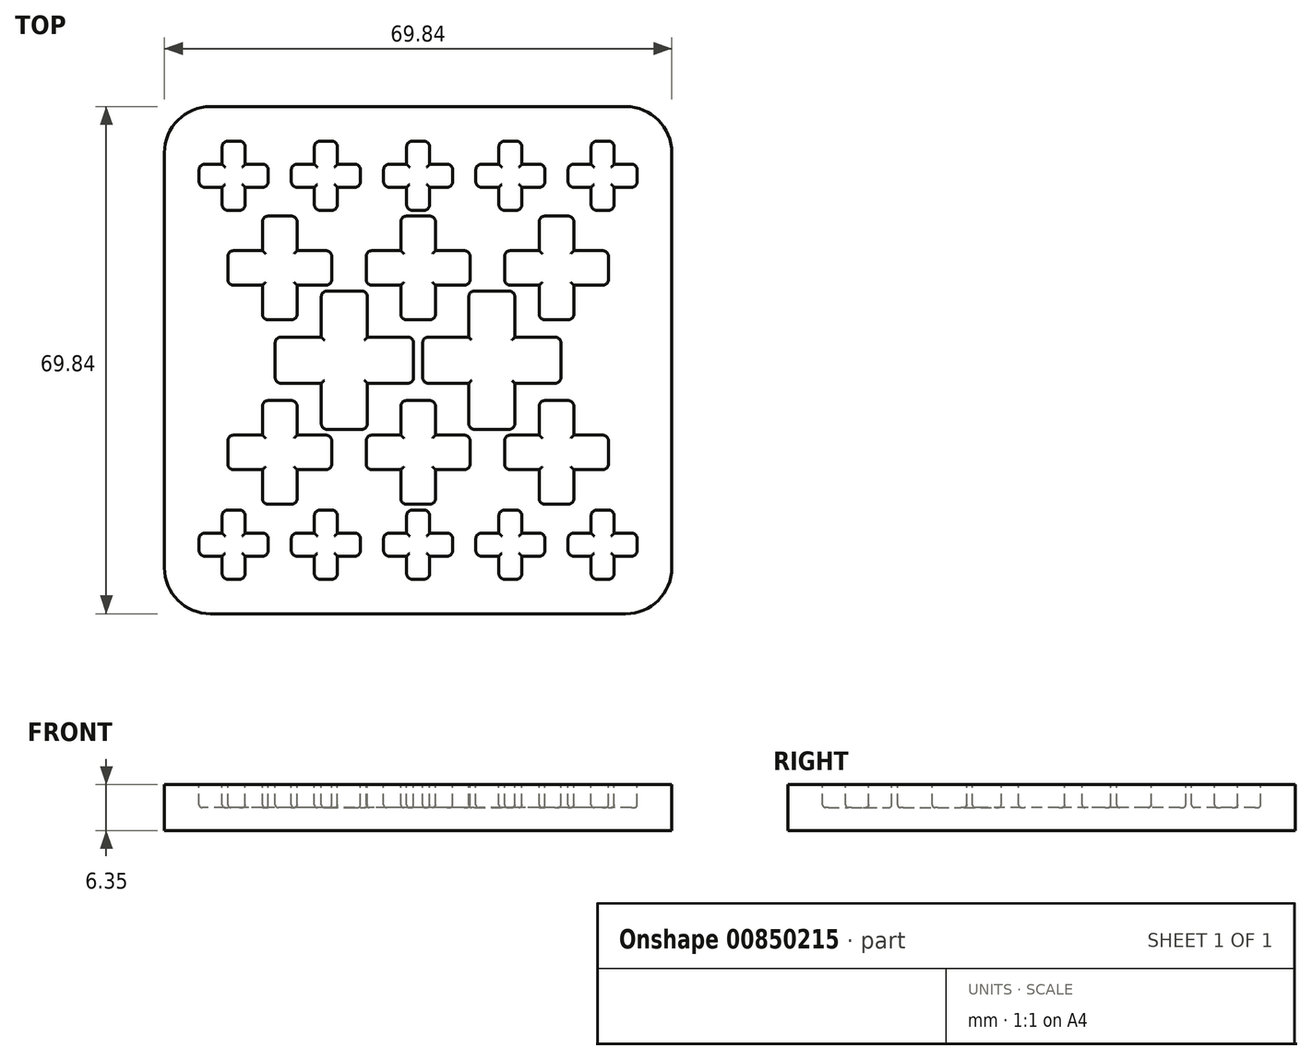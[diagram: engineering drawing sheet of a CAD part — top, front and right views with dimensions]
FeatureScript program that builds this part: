
annotation { "Feature Type Name" : "Feature", "Feature Type Description" : "" }
export const myFeature = defineFeature(function(context is Context, id is Id, definition is map)
    precondition{}
    {
        {
            var Q0;
            Q0=qCreatedBy(makeId("Top.planeOp"),FACE);
            var sketch = newSketch(context, id + "F0", { "sketchPlane" : qUnion([Q0])});
            skLineSegment(sketch, "E0.bottom", {"start": v(-28.57, 34.93) * mm, "end": v(28.58, 34.93) * mm});
            skLineSegment(sketch, "E0.top", {"start": v(-28.57, -34.93) * mm, "end": v(28.57, -34.93) * mm});
            skLineSegment(sketch, "E0.left", {"start": v(-34.92, 28.58) * mm, "end": v(-34.93, -28.57) * mm});
            skLineSegment(sketch, "E0.right", {"start": v(34.93, 28.58) * mm, "end": v(34.92, -28.57) * mm});
            skPoint(sketch, "E0.middle", {"position": v(0, 0) * mm});
            skPoint(sketch, "E1.visualSharp", {"position": v(-34.92, 34.93) * mm});
            skArc(sketch, "E1.filletArc", {"start": v(-28.57, 34.93) * mm, "mid": v(-33.07, 33.07) * mm, "end": v(-34.92, 28.58) * mm});
            skPoint(sketch, "E2.visualSharp", {"position": v(34.93, 34.93) * mm});
            skArc(sketch, "E2.filletArc", {"start": v(34.93, 28.58) * mm, "mid": v(33.07, 33.07) * mm, "end": v(28.58, 34.93) * mm});
            skPoint(sketch, "E3.visualSharp", {"position": v(34.92, -34.93) * mm});
            skArc(sketch, "E3.filletArc", {"start": v(28.57, -34.93) * mm, "mid": v(33.07, -33.07) * mm, "end": v(34.92, -28.57) * mm});
            skPoint(sketch, "E4.visualSharp", {"position": v(-34.93, -34.93) * mm});
            skArc(sketch, "E4.filletArc", {"start": v(-34.93, -28.57) * mm, "mid": v(-33.07, -33.07) * mm, "end": v(-28.57, -34.93) * mm});
            skSolve(sketch);
        }
        {
            var Q0;
            Q0 = qSketchRegion(id + "F0", true);
            extrude(context, id + "F1", {"entities" : qUnion([Q0]), "depth" : 6.35 * mm, "offsetDistance" : 25.4 * mm});
        }
        {
            var Q0;
            Q0=makeQuery(id+"F1.opExtrude","CAP_FACE",FACE,{"disambiguationData":[OSD([sQuery(id+"F0.wireOp",EDGE,"E0.bottom"),sQuery(id+"F0.wireOp",EDGE,"E0.top"),sQuery(id+"F0.wireOp",EDGE,"E0.left"),sQuery(id+"F0.wireOp",EDGE,"E0.right")])],"isStart":false});
            var sketch = newSketch(context, id + "F2", { "sketchPlane" : qUnion([Q0])});
            skLineSegment(sketch, "E5", {"start": v(0, 0) * mm, "end": v(0, 25.4) * mm, "construction": true});
            skLineSegment(sketch, "E6", {"start": v(0, 0) * mm, "end": v(0, 12.7) * mm, "construction": true});
            skLineSegment(sketch, "E7", {"start": v(0, 25.4) * mm, "end": v(-25.4, 25.4) * mm, "construction": true});
            skLineSegment(sketch, "E8", {"start": v(0, 12.7) * mm, "end": v(-19.05, 12.7) * mm, "construction": true});
            skLineSegment(sketch, "E9", {"start": v(0, 0) * mm, "end": v(-10.16, 0) * mm, "construction": true});
            skLineSegment(sketch, "E10.bottom", {"start": v(-24.6, 30.16) * mm, "end": v(-26.2, 30.16) * mm});
            skLineSegment(sketch, "E10.top", {"start": v(-24.6, 20.64) * mm, "end": v(-26.2, 20.64) * mm});
            skLineSegment(sketch, "E10.left", {"start": v(-23.81, 29.37) * mm, "end": v(-23.81, 21.43) * mm});
            skLineSegment(sketch, "E10.right", {"start": v(-26.99, 29.37) * mm, "end": v(-26.99, 21.43) * mm});
            skPoint(sketch, "E10.middle", {"position": v(-25.4, 25.4) * mm});
            skLineSegment(sketch, "E11.bottom", {"start": v(-21.43, 26.99) * mm, "end": v(-29.37, 26.99) * mm});
            skLineSegment(sketch, "E11.top", {"start": v(-21.43, 23.81) * mm, "end": v(-29.37, 23.81) * mm});
            skLineSegment(sketch, "E11.left", {"start": v(-20.64, 26.2) * mm, "end": v(-20.64, 24.6) * mm});
            skLineSegment(sketch, "E11.right", {"start": v(-30.16, 26.2) * mm, "end": v(-30.16, 24.6) * mm});
            skPoint(sketch, "E12.visualSharp", {"position": v(-26.99, 30.16) * mm});
            skArc(sketch, "E12.filletArc", {"start": v(-26.2, 30.16) * mm, "mid": v(-26.76, 29.93) * mm, "end": v(-26.99, 29.37) * mm});
            skPoint(sketch, "E13.visualSharp", {"position": v(-23.81, 30.16) * mm});
            skArc(sketch, "E13.filletArc", {"start": v(-23.81, 29.37) * mm, "mid": v(-24.04, 29.93) * mm, "end": v(-24.6, 30.16) * mm});
            skPoint(sketch, "E14.visualSharp", {"position": v(-20.64, 26.99) * mm});
            skArc(sketch, "E14.filletArc", {"start": v(-20.64, 26.2) * mm, "mid": v(-20.87, 26.76) * mm, "end": v(-21.43, 26.99) * mm});
            skPoint(sketch, "E15.visualSharp", {"position": v(-20.64, 23.81) * mm});
            skArc(sketch, "E15.filletArc", {"start": v(-21.43, 23.81) * mm, "mid": v(-20.87, 24.04) * mm, "end": v(-20.64, 24.6) * mm});
            skPoint(sketch, "E16.visualSharp", {"position": v(-23.81, 20.64) * mm});
            skArc(sketch, "E16.filletArc", {"start": v(-24.6, 20.64) * mm, "mid": v(-24.04, 20.87) * mm, "end": v(-23.81, 21.43) * mm});
            skPoint(sketch, "E17.visualSharp", {"position": v(-26.99, 20.64) * mm});
            skArc(sketch, "E17.filletArc", {"start": v(-26.99, 21.43) * mm, "mid": v(-26.76, 20.87) * mm, "end": v(-26.2, 20.64) * mm});
            skPoint(sketch, "E18.visualSharp", {"position": v(-30.16, 23.81) * mm});
            skArc(sketch, "E18.filletArc", {"start": v(-30.16, 24.6) * mm, "mid": v(-29.93, 24.04) * mm, "end": v(-29.37, 23.81) * mm});
            skPoint(sketch, "E19.visualSharp", {"position": v(-30.16, 26.99) * mm});
            skArc(sketch, "E19.filletArc", {"start": v(-29.37, 26.99) * mm, "mid": v(-29.93, 26.76) * mm, "end": v(-30.16, 26.2) * mm});
            skLineSegment(sketch, "E20.bottom", {"start": v(-17.46, 19.84) * mm, "end": v(-20.64, 19.84) * mm});
            skLineSegment(sketch, "E20.top", {"start": v(-17.46, 5.56) * mm, "end": v(-20.64, 5.56) * mm});
            skLineSegment(sketch, "E20.left", {"start": v(-16.67, 19.05) * mm, "end": v(-16.67, 6.35) * mm});
            skLineSegment(sketch, "E20.right", {"start": v(-21.43, 19.05) * mm, "end": v(-21.43, 6.35) * mm});
            skPoint(sketch, "E20.middle", {"position": v(-19.05, 12.7) * mm});
            skLineSegment(sketch, "E21.bottom", {"start": v(-12.7, 15.08) * mm, "end": v(-25.4, 15.08) * mm});
            skLineSegment(sketch, "E21.top", {"start": v(-12.7, 10.32) * mm, "end": v(-25.4, 10.32) * mm});
            skLineSegment(sketch, "E21.left", {"start": v(-11.9, 14.29) * mm, "end": v(-11.9, 11.11) * mm});
            skLineSegment(sketch, "E21.right", {"start": v(-26.2, 14.29) * mm, "end": v(-26.2, 11.11) * mm});
            skPoint(sketch, "E22.visualSharp", {"position": v(-21.43, 19.84) * mm});
            skArc(sketch, "E22.filletArc", {"start": v(-20.64, 19.84) * mm, "mid": v(-21.2, 19.61) * mm, "end": v(-21.43, 19.05) * mm});
            skPoint(sketch, "E23.visualSharp", {"position": v(-16.67, 19.84) * mm});
            skArc(sketch, "E23.filletArc", {"start": v(-16.67, 19.05) * mm, "mid": v(-16.9, 19.61) * mm, "end": v(-17.46, 19.84) * mm});
            skPoint(sketch, "E24.visualSharp", {"position": v(-11.9, 15.08) * mm});
            skArc(sketch, "E24.filletArc", {"start": v(-11.9, 14.29) * mm, "mid": v(-12.14, 14.85) * mm, "end": v(-12.7, 15.08) * mm});
            skPoint(sketch, "E25.visualSharp", {"position": v(-11.9, 10.32) * mm});
            skArc(sketch, "E25.filletArc", {"start": v(-12.7, 10.32) * mm, "mid": v(-12.14, 10.55) * mm, "end": v(-11.9, 11.11) * mm});
            skPoint(sketch, "E26.visualSharp", {"position": v(-16.67, 5.56) * mm});
            skArc(sketch, "E26.filletArc", {"start": v(-17.46, 5.56) * mm, "mid": v(-16.9, 5.79) * mm, "end": v(-16.67, 6.35) * mm});
            skPoint(sketch, "E27.visualSharp", {"position": v(-21.43, 5.56) * mm});
            skArc(sketch, "E27.filletArc", {"start": v(-21.43, 6.35) * mm, "mid": v(-21.2, 5.79) * mm, "end": v(-20.64, 5.56) * mm});
            skPoint(sketch, "E28.visualSharp", {"position": v(-26.2, 10.32) * mm});
            skArc(sketch, "E28.filletArc", {"start": v(-26.2, 11.11) * mm, "mid": v(-25.96, 10.55) * mm, "end": v(-25.4, 10.32) * mm});
            skPoint(sketch, "E29.visualSharp", {"position": v(-26.2, 15.08) * mm});
            skArc(sketch, "E29.filletArc", {"start": v(-25.4, 15.08) * mm, "mid": v(-25.96, 14.85) * mm, "end": v(-26.2, 14.29) * mm});
            skLineSegment(sketch, "E30.bottom", {"start": v(-12.54, 9.53) * mm, "end": v(-7.78, 9.53) * mm});
            skLineSegment(sketch, "E30.top", {"start": v(-12.54, -9.53) * mm, "end": v(-7.78, -9.53) * mm});
            skLineSegment(sketch, "E30.left", {"start": v(-13.34, 8.73) * mm, "end": v(-13.34, -8.73) * mm});
            skLineSegment(sketch, "E30.right", {"start": v(-6.99, 8.73) * mm, "end": v(-6.99, -8.73) * mm});
            skPoint(sketch, "E30.middle", {"position": v(-10.16, 0) * mm});
            skLineSegment(sketch, "E31.bottom", {"start": v(-1.43, 3.17) * mm, "end": v(-18.9, 3.18) * mm});
            skLineSegment(sketch, "E31.top", {"start": v(-1.43, -3.18) * mm, "end": v(-18.9, -3.17) * mm});
            skLineSegment(sketch, "E31.left", {"start": v(-0.64, 2.38) * mm, "end": v(-0.64, -2.38) * mm});
            skLineSegment(sketch, "E31.right", {"start": v(-19.69, 2.38) * mm, "end": v(-19.69, -2.38) * mm});
            skPoint(sketch, "E32.visualSharp", {"position": v(-13.34, 9.53) * mm});
            skArc(sketch, "E32.filletArc", {"start": v(-12.54, 9.52) * mm, "mid": v(-13.1, 9.3) * mm, "end": v(-13.33, 8.73) * mm});
            skPoint(sketch, "E33.visualSharp", {"position": v(-6.99, 9.53) * mm});
            skArc(sketch, "E33.filletArc", {"start": v(-6.99, 8.73) * mm, "mid": v(-7.22, 9.3) * mm, "end": v(-7.78, 9.52) * mm});
            skPoint(sketch, "E34.visualSharp", {"position": v(-0.64, 3.17) * mm});
            skArc(sketch, "E34.filletArc", {"start": v(-0.64, 2.38) * mm, "mid": v(-0.87, 2.94) * mm, "end": v(-1.43, 3.17) * mm});
            skPoint(sketch, "E35.visualSharp", {"position": v(-0.64, -3.18) * mm});
            skArc(sketch, "E35.filletArc", {"start": v(-1.43, -3.18) * mm, "mid": v(-0.87, -2.94) * mm, "end": v(-0.64, -2.38) * mm});
            skPoint(sketch, "E36.visualSharp", {"position": v(-6.99, -9.53) * mm});
            skArc(sketch, "E36.filletArc", {"start": v(-7.78, -9.52) * mm, "mid": v(-7.22, -9.3) * mm, "end": v(-6.99, -8.73) * mm});
            skPoint(sketch, "E37.visualSharp", {"position": v(-13.34, -9.53) * mm});
            skArc(sketch, "E37.filletArc", {"start": v(-13.34, -8.73) * mm, "mid": v(-13.1, -9.3) * mm, "end": v(-12.54, -9.52) * mm});
            skPoint(sketch, "E38.visualSharp", {"position": v(-19.69, -3.17) * mm});
            skArc(sketch, "E38.filletArc", {"start": v(-19.69, -2.38) * mm, "mid": v(-19.45, -2.94) * mm, "end": v(-18.9, -3.17) * mm});
            skPoint(sketch, "E39.visualSharp", {"position": v(-19.69, 3.18) * mm});
            skArc(sketch, "E39.filletArc", {"start": v(-18.9, 3.18) * mm, "mid": v(-19.45, 2.94) * mm, "end": v(-19.69, 2.38) * mm});
            skPoint(sketch, "E40.1.0.0", {"position": v(-7.94, 26.99) * mm});
            skLineSegment(sketch, "E40.1.0.1", {"start": v(-14.29, 29.37) * mm, "end": v(-14.29, 21.43) * mm});
            skLineSegment(sketch, "E40.1.0.2", {"start": v(-11.9, 30.16) * mm, "end": v(-13.5, 30.16) * mm});
            skPoint(sketch, "E40.1.0.3", {"position": v(-11.11, 30.16) * mm});
            skPoint(sketch, "E40.1.0.4", {"position": v(-14.29, 30.16) * mm});
            skPoint(sketch, "E40.1.0.5", {"position": v(-14.29, 20.64) * mm});
            skPoint(sketch, "E40.1.0.6", {"position": v(-17.46, 26.99) * mm});
            skPoint(sketch, "E40.1.0.7", {"position": v(-12.7, 25.4) * mm});
            skPoint(sketch, "E40.1.0.8", {"position": v(-11.11, 20.64) * mm});
            skLineSegment(sketch, "E40.1.0.9", {"start": v(-8.73, 26.99) * mm, "end": v(-16.67, 26.99) * mm});
            skLineSegment(sketch, "E40.1.0.10", {"start": v(-8.73, 23.81) * mm, "end": v(-16.67, 23.81) * mm});
            skLineSegment(sketch, "E40.1.0.11", {"start": v(-17.46, 26.2) * mm, "end": v(-17.46, 24.6) * mm});
            skLineSegment(sketch, "E40.1.0.12", {"start": v(-7.94, 26.2) * mm, "end": v(-7.94, 24.6) * mm});
            skPoint(sketch, "E40.1.0.13", {"position": v(-7.94, 23.81) * mm});
            skPoint(sketch, "E40.1.0.14", {"position": v(-17.46, 23.81) * mm});
            skLineSegment(sketch, "E40.1.0.15", {"start": v(-11.9, 20.64) * mm, "end": v(-13.5, 20.64) * mm});
            skLineSegment(sketch, "E40.1.0.16", {"start": v(-11.11, 29.37) * mm, "end": v(-11.11, 21.43) * mm});
            skPoint(sketch, "E40.1.0.17", {"position": v(-12.7, 25.4) * mm});
            skArc(sketch, "E40.1.0.18", {"start": v(-11.11, 29.37) * mm, "mid": v(-11.34, 29.93) * mm, "end": v(-11.9, 30.16) * mm});
            skArc(sketch, "E40.1.0.19", {"start": v(-8.73, 23.81) * mm, "mid": v(-8.17, 24.04) * mm, "end": v(-7.94, 24.6) * mm});
            skArc(sketch, "E40.1.0.20", {"start": v(-11.9, 20.64) * mm, "mid": v(-11.34, 20.87) * mm, "end": v(-11.11, 21.43) * mm});
            skArc(sketch, "E40.1.0.21", {"start": v(-14.29, 21.43) * mm, "mid": v(-14.06, 20.87) * mm, "end": v(-13.5, 20.64) * mm});
            skArc(sketch, "E40.1.0.22", {"start": v(-16.67, 26.99) * mm, "mid": v(-17.23, 26.76) * mm, "end": v(-17.46, 26.2) * mm});
            skArc(sketch, "E40.1.0.23", {"start": v(-17.46, 24.6) * mm, "mid": v(-17.23, 24.04) * mm, "end": v(-16.67, 23.81) * mm});
            skArc(sketch, "E40.1.0.24", {"start": v(-13.5, 30.16) * mm, "mid": v(-14.06, 29.93) * mm, "end": v(-14.29, 29.37) * mm});
            skArc(sketch, "E40.1.0.25", {"start": v(-7.94, 26.2) * mm, "mid": v(-8.17, 26.76) * mm, "end": v(-8.73, 26.99) * mm});
            skPoint(sketch, "E40.2.0.0", {"position": v(4.76, 26.99) * mm});
            skLineSegment(sketch, "E40.2.0.1", {"start": v(-1.59, 29.37) * mm, "end": v(-1.59, 21.43) * mm});
            skLineSegment(sketch, "E40.2.0.2", {"start": v(0.8, 30.16) * mm, "end": v(-0.8, 30.16) * mm});
            skPoint(sketch, "E40.2.0.3", {"position": v(1.59, 30.16) * mm});
            skPoint(sketch, "E40.2.0.4", {"position": v(-1.59, 30.16) * mm});
            skPoint(sketch, "E40.2.0.5", {"position": v(-1.59, 20.64) * mm});
            skPoint(sketch, "E40.2.0.6", {"position": v(-4.76, 26.99) * mm});
            skPoint(sketch, "E40.2.0.7", {"position": v(0, 25.4) * mm});
            skPoint(sketch, "E40.2.0.8", {"position": v(1.59, 20.64) * mm});
            skLineSegment(sketch, "E40.2.0.9", {"start": v(3.97, 26.99) * mm, "end": v(-3.97, 26.99) * mm});
            skLineSegment(sketch, "E40.2.0.10", {"start": v(3.97, 23.81) * mm, "end": v(-3.97, 23.81) * mm});
            skLineSegment(sketch, "E40.2.0.11", {"start": v(-4.76, 26.2) * mm, "end": v(-4.76, 24.6) * mm});
            skLineSegment(sketch, "E40.2.0.12", {"start": v(4.76, 26.2) * mm, "end": v(4.76, 24.6) * mm});
            skPoint(sketch, "E40.2.0.13", {"position": v(4.76, 23.81) * mm});
            skPoint(sketch, "E40.2.0.14", {"position": v(-4.76, 23.81) * mm});
            skLineSegment(sketch, "E40.2.0.15", {"start": v(0.8, 20.64) * mm, "end": v(-0.8, 20.64) * mm});
            skLineSegment(sketch, "E40.2.0.16", {"start": v(1.59, 29.37) * mm, "end": v(1.59, 21.43) * mm});
            skPoint(sketch, "E40.2.0.17", {"position": v(0, 25.4) * mm});
            skArc(sketch, "E40.2.0.18", {"start": v(1.59, 29.37) * mm, "mid": v(1.36, 29.93) * mm, "end": v(0.8, 30.16) * mm});
            skArc(sketch, "E40.2.0.19", {"start": v(3.97, 23.81) * mm, "mid": v(4.53, 24.04) * mm, "end": v(4.76, 24.6) * mm});
            skArc(sketch, "E40.2.0.20", {"start": v(0.8, 20.64) * mm, "mid": v(1.36, 20.87) * mm, "end": v(1.59, 21.43) * mm});
            skArc(sketch, "E40.2.0.21", {"start": v(-1.59, 21.43) * mm, "mid": v(-1.36, 20.87) * mm, "end": v(-0.8, 20.64) * mm});
            skArc(sketch, "E40.2.0.22", {"start": v(-3.97, 26.99) * mm, "mid": v(-4.53, 26.76) * mm, "end": v(-4.76, 26.2) * mm});
            skArc(sketch, "E40.2.0.23", {"start": v(-4.76, 24.6) * mm, "mid": v(-4.53, 24.04) * mm, "end": v(-3.97, 23.81) * mm});
            skArc(sketch, "E40.2.0.24", {"start": v(-0.8, 30.16) * mm, "mid": v(-1.36, 29.93) * mm, "end": v(-1.59, 29.37) * mm});
            skArc(sketch, "E40.2.0.25", {"start": v(4.76, 26.2) * mm, "mid": v(4.53, 26.76) * mm, "end": v(3.97, 26.99) * mm});
            skPoint(sketch, "E40.3.0.0", {"position": v(17.46, 26.99) * mm});
            skLineSegment(sketch, "E40.3.0.1", {"start": v(11.11, 29.37) * mm, "end": v(11.11, 21.43) * mm});
            skLineSegment(sketch, "E40.3.0.2", {"start": v(13.5, 30.16) * mm, "end": v(11.9, 30.16) * mm});
            skPoint(sketch, "E40.3.0.3", {"position": v(14.29, 30.16) * mm});
            skPoint(sketch, "E40.3.0.4", {"position": v(11.11, 30.16) * mm});
            skPoint(sketch, "E40.3.0.5", {"position": v(11.11, 20.64) * mm});
            skPoint(sketch, "E40.3.0.6", {"position": v(7.94, 26.99) * mm});
            skPoint(sketch, "E40.3.0.7", {"position": v(12.7, 25.4) * mm});
            skPoint(sketch, "E40.3.0.8", {"position": v(14.29, 20.64) * mm});
            skLineSegment(sketch, "E40.3.0.9", {"start": v(16.67, 26.99) * mm, "end": v(8.73, 26.99) * mm});
            skLineSegment(sketch, "E40.3.0.10", {"start": v(16.67, 23.81) * mm, "end": v(8.73, 23.81) * mm});
            skLineSegment(sketch, "E40.3.0.11", {"start": v(7.94, 26.2) * mm, "end": v(7.94, 24.6) * mm});
            skLineSegment(sketch, "E40.3.0.12", {"start": v(17.46, 26.2) * mm, "end": v(17.46, 24.6) * mm});
            skPoint(sketch, "E40.3.0.13", {"position": v(17.46, 23.81) * mm});
            skPoint(sketch, "E40.3.0.14", {"position": v(7.94, 23.81) * mm});
            skLineSegment(sketch, "E40.3.0.15", {"start": v(13.5, 20.64) * mm, "end": v(11.9, 20.64) * mm});
            skLineSegment(sketch, "E40.3.0.16", {"start": v(14.29, 29.37) * mm, "end": v(14.29, 21.43) * mm});
            skPoint(sketch, "E40.3.0.17", {"position": v(12.7, 25.4) * mm});
            skArc(sketch, "E40.3.0.18", {"start": v(14.29, 29.37) * mm, "mid": v(14.06, 29.93) * mm, "end": v(13.5, 30.16) * mm});
            skArc(sketch, "E40.3.0.19", {"start": v(16.67, 23.81) * mm, "mid": v(17.23, 24.04) * mm, "end": v(17.46, 24.6) * mm});
            skArc(sketch, "E40.3.0.20", {"start": v(13.5, 20.64) * mm, "mid": v(14.06, 20.87) * mm, "end": v(14.29, 21.43) * mm});
            skArc(sketch, "E40.3.0.21", {"start": v(11.11, 21.43) * mm, "mid": v(11.34, 20.87) * mm, "end": v(11.9, 20.64) * mm});
            skArc(sketch, "E40.3.0.22", {"start": v(8.73, 26.99) * mm, "mid": v(8.17, 26.76) * mm, "end": v(7.94, 26.2) * mm});
            skArc(sketch, "E40.3.0.23", {"start": v(7.94, 24.6) * mm, "mid": v(8.17, 24.04) * mm, "end": v(8.73, 23.81) * mm});
            skArc(sketch, "E40.3.0.24", {"start": v(11.9, 30.16) * mm, "mid": v(11.34, 29.93) * mm, "end": v(11.11, 29.37) * mm});
            skArc(sketch, "E40.3.0.25", {"start": v(17.46, 26.2) * mm, "mid": v(17.23, 26.76) * mm, "end": v(16.67, 26.99) * mm});
            skPoint(sketch, "E40.4.0.0", {"position": v(30.16, 26.99) * mm});
            skLineSegment(sketch, "E40.4.0.1", {"start": v(23.81, 29.37) * mm, "end": v(23.81, 21.43) * mm});
            skLineSegment(sketch, "E40.4.0.2", {"start": v(26.2, 30.16) * mm, "end": v(24.6, 30.16) * mm});
            skPoint(sketch, "E40.4.0.3", {"position": v(26.99, 30.16) * mm});
            skPoint(sketch, "E40.4.0.4", {"position": v(23.81, 30.16) * mm});
            skPoint(sketch, "E40.4.0.5", {"position": v(23.81, 20.64) * mm});
            skPoint(sketch, "E40.4.0.6", {"position": v(20.64, 26.99) * mm});
            skPoint(sketch, "E40.4.0.7", {"position": v(25.4, 25.4) * mm});
            skPoint(sketch, "E40.4.0.8", {"position": v(26.99, 20.64) * mm});
            skLineSegment(sketch, "E40.4.0.9", {"start": v(29.37, 26.99) * mm, "end": v(21.43, 26.99) * mm});
            skLineSegment(sketch, "E40.4.0.10", {"start": v(29.37, 23.81) * mm, "end": v(21.43, 23.81) * mm});
            skLineSegment(sketch, "E40.4.0.11", {"start": v(20.64, 26.2) * mm, "end": v(20.64, 24.6) * mm});
            skLineSegment(sketch, "E40.4.0.12", {"start": v(30.16, 26.2) * mm, "end": v(30.16, 24.6) * mm});
            skPoint(sketch, "E40.4.0.13", {"position": v(30.16, 23.81) * mm});
            skPoint(sketch, "E40.4.0.14", {"position": v(20.64, 23.81) * mm});
            skLineSegment(sketch, "E40.4.0.15", {"start": v(26.2, 20.64) * mm, "end": v(24.6, 20.64) * mm});
            skLineSegment(sketch, "E40.4.0.16", {"start": v(26.99, 29.37) * mm, "end": v(26.99, 21.43) * mm});
            skPoint(sketch, "E40.4.0.17", {"position": v(25.4, 25.4) * mm});
            skArc(sketch, "E40.4.0.18", {"start": v(26.99, 29.37) * mm, "mid": v(26.76, 29.93) * mm, "end": v(26.2, 30.16) * mm});
            skArc(sketch, "E40.4.0.19", {"start": v(29.37, 23.81) * mm, "mid": v(29.93, 24.04) * mm, "end": v(30.16, 24.6) * mm});
            skArc(sketch, "E40.4.0.20", {"start": v(26.2, 20.64) * mm, "mid": v(26.76, 20.87) * mm, "end": v(26.99, 21.43) * mm});
            skArc(sketch, "E40.4.0.21", {"start": v(23.81, 21.43) * mm, "mid": v(24.04, 20.87) * mm, "end": v(24.6, 20.64) * mm});
            skArc(sketch, "E40.4.0.22", {"start": v(21.43, 26.99) * mm, "mid": v(20.87, 26.76) * mm, "end": v(20.64, 26.2) * mm});
            skArc(sketch, "E40.4.0.23", {"start": v(20.64, 24.6) * mm, "mid": v(20.87, 24.04) * mm, "end": v(21.43, 23.81) * mm});
            skArc(sketch, "E40.4.0.24", {"start": v(24.6, 30.16) * mm, "mid": v(24.04, 29.93) * mm, "end": v(23.81, 29.37) * mm});
            skArc(sketch, "E40.4.0.25", {"start": v(30.16, 26.2) * mm, "mid": v(29.93, 26.76) * mm, "end": v(29.37, 26.99) * mm});
            skLineSegment(sketch, "E40.direction1", {"start": v(-26.99, 20.64) * mm, "end": v(-14.29, 20.64) * mm, "construction": true});
            skPoint(sketch, "E41.1.0.0", {"position": v(4.76, 20.64) * mm});
            skLineSegment(sketch, "E41.1.0.1", {"start": v(1.59, 5.56) * mm, "end": v(-1.59, 5.56) * mm});
            skLineSegment(sketch, "E41.1.0.2", {"start": v(6.35, 10.32) * mm, "end": v(-6.35, 10.32) * mm});
            skPoint(sketch, "E41.1.0.3", {"position": v(2.38, 5.56) * mm});
            skPoint(sketch, "E41.1.0.4", {"position": v(7.94, 20.64) * mm});
            skPoint(sketch, "E41.1.0.5", {"position": v(-7.94, 20.64) * mm});
            skPoint(sketch, "E41.1.0.6", {"position": v(0, 12.7) * mm});
            skLineSegment(sketch, "E41.1.0.7", {"start": v(6.35, 15.08) * mm, "end": v(-6.35, 15.08) * mm});
            skPoint(sketch, "E41.1.0.8", {"position": v(7.14, 15.08) * mm});
            skLineSegment(sketch, "E41.1.0.9", {"start": v(1.59, 19.84) * mm, "end": v(-1.59, 19.84) * mm});
            skArc(sketch, "E41.1.0.10", {"start": v(2.38, 19.05) * mm, "mid": v(2.15, 19.61) * mm, "end": v(1.59, 19.84) * mm});
            skLineSegment(sketch, "E41.1.0.11", {"start": v(-2.38, 19.05) * mm, "end": v(-2.38, 6.35) * mm});
            skPoint(sketch, "E41.1.0.12", {"position": v(-7.14, 15.08) * mm});
            skPoint(sketch, "E41.1.0.13", {"position": v(7.14, 10.32) * mm});
            skPoint(sketch, "E41.1.0.14", {"position": v(-7.14, 10.32) * mm});
            skPoint(sketch, "E41.1.0.15", {"position": v(-2.38, 5.56) * mm});
            skLineSegment(sketch, "E41.1.0.16", {"start": v(7.14, 14.29) * mm, "end": v(7.14, 11.11) * mm});
            skPoint(sketch, "E41.1.0.17", {"position": v(-4.76, 20.64) * mm});
            skLineSegment(sketch, "E41.1.0.18", {"start": v(-7.14, 14.29) * mm, "end": v(-7.14, 11.11) * mm});
            skLineSegment(sketch, "E41.1.0.19", {"start": v(2.38, 19.05) * mm, "end": v(2.38, 6.35) * mm});
            skArc(sketch, "E41.1.0.20", {"start": v(-1.59, 19.84) * mm, "mid": v(-2.15, 19.61) * mm, "end": v(-2.38, 19.05) * mm});
            skPoint(sketch, "E41.1.0.21", {"position": v(0, 12.7) * mm});
            skArc(sketch, "E41.1.0.22", {"start": v(7.14, 14.29) * mm, "mid": v(6.91, 14.85) * mm, "end": v(6.35, 15.08) * mm});
            skArc(sketch, "E41.1.0.23", {"start": v(-7.14, 11.11) * mm, "mid": v(-6.91, 10.55) * mm, "end": v(-6.35, 10.32) * mm});
            skArc(sketch, "E41.1.0.24", {"start": v(-2.38, 6.35) * mm, "mid": v(-2.15, 5.79) * mm, "end": v(-1.59, 5.56) * mm});
            skArc(sketch, "E41.1.0.25", {"start": v(1.59, 5.56) * mm, "mid": v(2.15, 5.79) * mm, "end": v(2.38, 6.35) * mm});
            skArc(sketch, "E41.1.0.26", {"start": v(6.35, 10.32) * mm, "mid": v(6.91, 10.55) * mm, "end": v(7.14, 11.11) * mm});
            skArc(sketch, "E41.1.0.27", {"start": v(-6.35, 15.08) * mm, "mid": v(-6.91, 14.85) * mm, "end": v(-7.14, 14.29) * mm});
            skLineSegment(sketch, "E41.2.0.1", {"start": v(20.64, 5.56) * mm, "end": v(17.46, 5.56) * mm});
            skLineSegment(sketch, "E41.2.0.2", {"start": v(25.4, 10.32) * mm, "end": v(12.7, 10.32) * mm});
            skPoint(sketch, "E41.2.0.3", {"position": v(21.43, 5.56) * mm});
            skPoint(sketch, "E41.2.0.6", {"position": v(19.05, 12.7) * mm});
            skLineSegment(sketch, "E41.2.0.7", {"start": v(25.4, 15.08) * mm, "end": v(12.7, 15.08) * mm});
            skPoint(sketch, "E41.2.0.8", {"position": v(26.2, 15.08) * mm});
            skLineSegment(sketch, "E41.2.0.9", {"start": v(20.64, 19.84) * mm, "end": v(17.46, 19.84) * mm});
            skArc(sketch, "E41.2.0.10", {"start": v(21.43, 19.05) * mm, "mid": v(21.2, 19.61) * mm, "end": v(20.64, 19.84) * mm});
            skLineSegment(sketch, "E41.2.0.11", {"start": v(16.67, 19.05) * mm, "end": v(16.67, 6.35) * mm});
            skPoint(sketch, "E41.2.0.12", {"position": v(11.9, 15.08) * mm});
            skPoint(sketch, "E41.2.0.13", {"position": v(26.2, 10.32) * mm});
            skPoint(sketch, "E41.2.0.14", {"position": v(11.9, 10.32) * mm});
            skPoint(sketch, "E41.2.0.15", {"position": v(16.67, 5.56) * mm});
            skLineSegment(sketch, "E41.2.0.16", {"start": v(26.2, 14.29) * mm, "end": v(26.2, 11.11) * mm});
            skLineSegment(sketch, "E41.2.0.18", {"start": v(11.9, 14.29) * mm, "end": v(11.9, 11.11) * mm});
            skLineSegment(sketch, "E41.2.0.19", {"start": v(21.43, 19.05) * mm, "end": v(21.43, 6.35) * mm});
            skArc(sketch, "E41.2.0.20", {"start": v(17.46, 19.84) * mm, "mid": v(16.9, 19.61) * mm, "end": v(16.67, 19.05) * mm});
            skPoint(sketch, "E41.2.0.21", {"position": v(19.05, 12.7) * mm});
            skArc(sketch, "E41.2.0.22", {"start": v(26.2, 14.29) * mm, "mid": v(25.96, 14.85) * mm, "end": v(25.4, 15.08) * mm});
            skArc(sketch, "E41.2.0.23", {"start": v(11.9, 11.11) * mm, "mid": v(12.14, 10.55) * mm, "end": v(12.7, 10.32) * mm});
            skArc(sketch, "E41.2.0.24", {"start": v(16.67, 6.35) * mm, "mid": v(16.9, 5.79) * mm, "end": v(17.46, 5.56) * mm});
            skArc(sketch, "E41.2.0.25", {"start": v(20.64, 5.56) * mm, "mid": v(21.2, 5.79) * mm, "end": v(21.43, 6.35) * mm});
            skArc(sketch, "E41.2.0.26", {"start": v(25.4, 10.32) * mm, "mid": v(25.96, 10.55) * mm, "end": v(26.2, 11.11) * mm});
            skArc(sketch, "E41.2.0.27", {"start": v(12.7, 15.08) * mm, "mid": v(12.14, 14.85) * mm, "end": v(11.9, 14.29) * mm});
            skLineSegment(sketch, "E41.direction1", {"start": v(-21.43, 5.56) * mm, "end": v(-2.38, 5.56) * mm, "construction": true});
            skLineSegment(sketch, "E42.1.0.0", {"start": v(13.3, 8.73) * mm, "end": v(13.3, -8.73) * mm});
            skArc(sketch, "E42.1.0.1", {"start": v(13.3, 8.73) * mm, "mid": v(13.08, 9.3) * mm, "end": v(12.52, 9.52) * mm});
            skLineSegment(sketch, "E42.1.0.2", {"start": v(7.75, 9.53) * mm, "end": v(12.52, 9.53) * mm});
            skArc(sketch, "E42.1.0.3", {"start": v(7.75, 9.52) * mm, "mid": v(7.2, 9.3) * mm, "end": v(6.96, 8.73) * mm});
            skLineSegment(sketch, "E42.1.0.4", {"start": v(6.96, 8.73) * mm, "end": v(6.96, -8.73) * mm});
            skLineSegment(sketch, "E42.1.0.5", {"start": v(18.87, 3.17) * mm, "end": v(1.4, 3.18) * mm});
            skArc(sketch, "E42.1.0.6", {"start": v(1.4, 3.18) * mm, "mid": v(0.84, 2.94) * mm, "end": v(0.6, 2.38) * mm});
            skLineSegment(sketch, "E42.1.0.7", {"start": v(0.6, 2.38) * mm, "end": v(0.6, -2.38) * mm});
            skArc(sketch, "E42.1.0.8", {"start": v(0.6, -2.38) * mm, "mid": v(0.84, -2.94) * mm, "end": v(1.4, -3.17) * mm});
            skLineSegment(sketch, "E42.1.0.9", {"start": v(18.87, -3.18) * mm, "end": v(1.4, -3.17) * mm});
            skArc(sketch, "E42.1.0.10", {"start": v(6.96, -8.73) * mm, "mid": v(7.2, -9.3) * mm, "end": v(7.75, -9.52) * mm});
            skLineSegment(sketch, "E42.1.0.11", {"start": v(7.75, -9.53) * mm, "end": v(12.52, -9.53) * mm});
            skArc(sketch, "E42.1.0.12", {"start": v(12.52, -9.52) * mm, "mid": v(13.08, -9.3) * mm, "end": v(13.3, -8.73) * mm});
            skArc(sketch, "E42.1.0.13", {"start": v(18.87, -3.18) * mm, "mid": v(19.43, -2.94) * mm, "end": v(19.66, -2.38) * mm});
            skLineSegment(sketch, "E42.1.0.14", {"start": v(19.66, 2.38) * mm, "end": v(19.66, -2.38) * mm});
            skArc(sketch, "E42.1.0.15", {"start": v(19.66, 2.38) * mm, "mid": v(19.43, 2.94) * mm, "end": v(18.87, 3.17) * mm});
            skLineSegment(sketch, "E42.direction1", {"start": v(-12.54, -9.53) * mm, "end": v(7.75, -9.53) * mm, "construction": true});
            skArc(sketch, "E43.MirrorCS", {"start": v(-12.54, -9.52) * mm, "mid": v(-13.1, -9.3) * mm, "end": v(-13.33, -8.73) * mm});
            skArc(sketch, "E44.MirrorCS", {"start": v(-26.2, -11.11) * mm, "mid": v(-25.96, -10.55) * mm, "end": v(-25.4, -10.32) * mm});
            skArc(sketch, "E45.MirrorCS", {"start": v(-7.78, 9.52) * mm, "mid": v(-7.22, 9.3) * mm, "end": v(-6.99, 8.73) * mm});
            skArc(sketch, "E46.MirrorCS", {"start": v(-26.2, -30.16) * mm, "mid": v(-26.76, -29.93) * mm, "end": v(-26.99, -29.37) * mm});
            skArc(sketch, "E47.MirrorCS", {"start": v(-11.11, -29.37) * mm, "mid": v(-11.34, -29.93) * mm, "end": v(-11.9, -30.16) * mm});
            skArc(sketch, "E48.MirrorCS", {"start": v(29.37, -23.81) * mm, "mid": v(29.93, -24.04) * mm, "end": v(30.16, -24.6) * mm});
            skArc(sketch, "E49.MirrorCS", {"start": v(-11.9, -14.29) * mm, "mid": v(-12.14, -14.85) * mm, "end": v(-12.7, -15.08) * mm});
            skArc(sketch, "E50.MirrorCS", {"start": v(-1.43, 3.18) * mm, "mid": v(-0.87, 2.94) * mm, "end": v(-0.64, 2.38) * mm});
            skArc(sketch, "E51.MirrorCS", {"start": v(-1.59, -19.84) * mm, "mid": v(-2.15, -19.61) * mm, "end": v(-2.38, -19.05) * mm});
            skArc(sketch, "E52.MirrorCS", {"start": v(-17.46, -24.6) * mm, "mid": v(-17.23, -24.04) * mm, "end": v(-16.67, -23.81) * mm});
            skArc(sketch, "E53.MirrorCS", {"start": v(-2.38, -6.35) * mm, "mid": v(-2.15, -5.79) * mm, "end": v(-1.59, -5.56) * mm});
            skArc(sketch, "E54.MirrorCS", {"start": v(-29.37, -26.99) * mm, "mid": v(-29.93, -26.76) * mm, "end": v(-30.16, -26.2) * mm});
            skArc(sketch, "E55.MirrorCS", {"start": v(-20.64, -26.2) * mm, "mid": v(-20.87, -26.76) * mm, "end": v(-21.43, -26.99) * mm});
            skArc(sketch, "E56.MirrorCS", {"start": v(11.9, -30.16) * mm, "mid": v(11.34, -29.93) * mm, "end": v(11.11, -29.37) * mm});
            skArc(sketch, "E57.MirrorCS", {"start": v(1.4, -3.18) * mm, "mid": v(0.84, -2.94) * mm, "end": v(0.6, -2.38) * mm});
            skArc(sketch, "E58.MirrorCS", {"start": v(0.6, 2.38) * mm, "mid": v(0.84, 2.94) * mm, "end": v(1.4, 3.17) * mm});
            skArc(sketch, "E59.MirrorCS", {"start": v(24.6, -30.16) * mm, "mid": v(24.04, -29.93) * mm, "end": v(23.81, -29.37) * mm});
            skArc(sketch, "E60.MirrorCS", {"start": v(-17.46, -5.56) * mm, "mid": v(-16.9, -5.79) * mm, "end": v(-16.67, -6.35) * mm});
            skArc(sketch, "E61.MirrorCS", {"start": v(-8.73, -23.81) * mm, "mid": v(-8.17, -24.04) * mm, "end": v(-7.94, -24.6) * mm});
            skArc(sketch, "E62.MirrorCS", {"start": v(-25.4, -15.08) * mm, "mid": v(-25.96, -14.85) * mm, "end": v(-26.2, -14.29) * mm});
            skArc(sketch, "E63.MirrorCS", {"start": v(-12.7, -10.32) * mm, "mid": v(-12.14, -10.55) * mm, "end": v(-11.9, -11.11) * mm});
            skArc(sketch, "E64.MirrorCS", {"start": v(26.99, -29.37) * mm, "mid": v(26.76, -29.93) * mm, "end": v(26.2, -30.16) * mm});
            skArc(sketch, "E65.MirrorCS", {"start": v(-23.81, -29.37) * mm, "mid": v(-24.04, -29.93) * mm, "end": v(-24.6, -30.16) * mm});
            skArc(sketch, "E66.MirrorCS", {"start": v(-6.35, -15.08) * mm, "mid": v(-6.91, -14.85) * mm, "end": v(-7.14, -14.29) * mm});
            skArc(sketch, "E67.MirrorCS", {"start": v(17.46, -26.2) * mm, "mid": v(17.23, -26.76) * mm, "end": v(16.67, -26.99) * mm});
            skArc(sketch, "E68.MirrorCS", {"start": v(16.67, -23.81) * mm, "mid": v(17.23, -24.04) * mm, "end": v(17.46, -24.6) * mm});
            skArc(sketch, "E69.MirrorCS", {"start": v(-0.8, -30.16) * mm, "mid": v(-1.36, -29.93) * mm, "end": v(-1.59, -29.37) * mm});
            skArc(sketch, "E70.MirrorCS", {"start": v(-13.5, -30.16) * mm, "mid": v(-14.06, -29.93) * mm, "end": v(-14.29, -29.37) * mm});
            skArc(sketch, "E71.MirrorCS", {"start": v(26.2, -20.64) * mm, "mid": v(26.76, -20.87) * mm, "end": v(26.99, -21.43) * mm});
            skArc(sketch, "E72.MirrorCS", {"start": v(13.3, -8.73) * mm, "mid": v(13.08, -9.3) * mm, "end": v(12.52, -9.52) * mm});
            skArc(sketch, "E73.MirrorCS", {"start": v(13.5, -20.64) * mm, "mid": v(14.06, -20.87) * mm, "end": v(14.29, -21.43) * mm});
            skArc(sketch, "E74.MirrorCS", {"start": v(-16.67, -19.05) * mm, "mid": v(-16.9, -19.61) * mm, "end": v(-17.46, -19.84) * mm});
            skArc(sketch, "E75.MirrorCS", {"start": v(25.4, -10.32) * mm, "mid": v(25.96, -10.55) * mm, "end": v(26.2, -11.11) * mm});
            skArc(sketch, "E76.MirrorCS", {"start": v(8.73, -26.99) * mm, "mid": v(8.17, -26.76) * mm, "end": v(7.94, -26.2) * mm});
            skArc(sketch, "E77.MirrorCS", {"start": v(12.7, -15.08) * mm, "mid": v(12.14, -14.85) * mm, "end": v(11.9, -14.29) * mm});
            skArc(sketch, "E78.MirrorCS", {"start": v(-3.97, -26.99) * mm, "mid": v(-4.53, -26.76) * mm, "end": v(-4.76, -26.2) * mm});
            skArc(sketch, "E79.MirrorCS", {"start": v(-16.67, -26.99) * mm, "mid": v(-17.23, -26.76) * mm, "end": v(-17.46, -26.2) * mm});
            skArc(sketch, "E80.MirrorCS", {"start": v(30.16, -26.2) * mm, "mid": v(29.93, -26.76) * mm, "end": v(29.37, -26.99) * mm});
            skArc(sketch, "E81.MirrorCS", {"start": v(14.29, -29.37) * mm, "mid": v(14.06, -29.93) * mm, "end": v(13.5, -30.16) * mm});
            skArc(sketch, "E82.MirrorCS", {"start": v(11.11, -21.43) * mm, "mid": v(11.34, -20.87) * mm, "end": v(11.9, -20.64) * mm});
            skArc(sketch, "E83.MirrorCS", {"start": v(-21.43, -6.35) * mm, "mid": v(-21.2, -5.79) * mm, "end": v(-20.64, -5.56) * mm});
            skArc(sketch, "E84.MirrorCS", {"start": v(20.64, -5.56) * mm, "mid": v(21.2, -5.79) * mm, "end": v(21.43, -6.35) * mm});
            skArc(sketch, "E85.MirrorCS", {"start": v(12.52, 9.52) * mm, "mid": v(13.08, 9.3) * mm, "end": v(13.3, 8.73) * mm});
            skArc(sketch, "E86.MirrorCS", {"start": v(-14.29, -21.43) * mm, "mid": v(-14.06, -20.87) * mm, "end": v(-13.5, -20.64) * mm});
            skArc(sketch, "E87.MirrorCS", {"start": v(-0.64, -2.38) * mm, "mid": v(-0.87, -2.94) * mm, "end": v(-1.43, -3.17) * mm});
            skArc(sketch, "E88.MirrorCS", {"start": v(23.81, -21.43) * mm, "mid": v(24.04, -20.87) * mm, "end": v(24.6, -20.64) * mm});
            skArc(sketch, "E89.MirrorCS", {"start": v(7.14, -14.29) * mm, "mid": v(6.91, -14.85) * mm, "end": v(6.35, -15.08) * mm});
            skArc(sketch, "E90.MirrorCS", {"start": v(-7.94, -26.2) * mm, "mid": v(-8.17, -26.76) * mm, "end": v(-8.73, -26.99) * mm});
            skArc(sketch, "E91.MirrorCS", {"start": v(4.76, -26.2) * mm, "mid": v(4.53, -26.76) * mm, "end": v(3.97, -26.99) * mm});
            skArc(sketch, "E92.MirrorCS", {"start": v(-30.16, -24.6) * mm, "mid": v(-29.93, -24.04) * mm, "end": v(-29.37, -23.81) * mm});
            skArc(sketch, "E93.MirrorCS", {"start": v(3.97, -23.81) * mm, "mid": v(4.53, -24.04) * mm, "end": v(4.76, -24.6) * mm});
            skArc(sketch, "E94.MirrorCS", {"start": v(-13.34, 8.73) * mm, "mid": v(-13.1, 9.3) * mm, "end": v(-12.54, 9.52) * mm});
            skArc(sketch, "E95.MirrorCS", {"start": v(-20.64, -19.84) * mm, "mid": v(-21.2, -19.61) * mm, "end": v(-21.43, -19.05) * mm});
            skArc(sketch, "E96.MirrorCS", {"start": v(-7.14, -11.11) * mm, "mid": v(-6.91, -10.55) * mm, "end": v(-6.35, -10.32) * mm});
            skArc(sketch, "E97.MirrorCS", {"start": v(21.43, -26.99) * mm, "mid": v(20.87, -26.76) * mm, "end": v(20.64, -26.2) * mm});
            skArc(sketch, "E98.MirrorCS", {"start": v(26.2, -14.29) * mm, "mid": v(25.96, -14.85) * mm, "end": v(25.4, -15.08) * mm});
            skArc(sketch, "E99.MirrorCS", {"start": v(6.96, 8.73) * mm, "mid": v(7.2, 9.3) * mm, "end": v(7.75, 9.52) * mm});
            skArc(sketch, "E100.MirrorCS", {"start": v(-26.99, -21.43) * mm, "mid": v(-26.76, -20.87) * mm, "end": v(-26.2, -20.64) * mm});
            skArc(sketch, "E101.MirrorCS", {"start": v(21.43, -19.05) * mm, "mid": v(21.2, -19.61) * mm, "end": v(20.64, -19.84) * mm});
            skArc(sketch, "E102.MirrorCS", {"start": v(1.59, -29.37) * mm, "mid": v(1.36, -29.93) * mm, "end": v(0.8, -30.16) * mm});
            skArc(sketch, "E103.MirrorCS", {"start": v(7.94, -24.6) * mm, "mid": v(8.17, -24.04) * mm, "end": v(8.73, -23.81) * mm});
            skArc(sketch, "E104.MirrorCS", {"start": v(11.9, -11.11) * mm, "mid": v(12.14, -10.55) * mm, "end": v(12.7, -10.32) * mm});
            skArc(sketch, "E105.MirrorCS", {"start": v(0.8, -20.64) * mm, "mid": v(1.36, -20.87) * mm, "end": v(1.59, -21.43) * mm});
            skArc(sketch, "E106.MirrorCS", {"start": v(-11.9, -20.64) * mm, "mid": v(-11.34, -20.87) * mm, "end": v(-11.11, -21.43) * mm});
            skLineSegment(sketch, "E107.MirrorCS", {"start": v(0.8, -20.64) * mm, "end": v(-0.8, -20.64) * mm});
            skArc(sketch, "E108.MirrorCS", {"start": v(16.67, -6.35) * mm, "mid": v(16.9, -5.79) * mm, "end": v(17.46, -5.56) * mm});
            skArc(sketch, "E109.MirrorCS", {"start": v(20.64, -24.6) * mm, "mid": v(20.87, -24.04) * mm, "end": v(21.43, -23.81) * mm});
            skPoint(sketch, "E110.MirrorP", {"position": v(12.7, -25.4) * mm});
            skArc(sketch, "E111.MirrorCS", {"start": v(-18.9, -3.18) * mm, "mid": v(-19.45, -2.94) * mm, "end": v(-19.69, -2.38) * mm});
            skPoint(sketch, "E112.MirrorP", {"position": v(-25.4, -25.4) * mm});
            skArc(sketch, "E113.MirrorCS", {"start": v(-6.99, -8.73) * mm, "mid": v(-7.22, -9.3) * mm, "end": v(-7.78, -9.52) * mm});
            skLineSegment(sketch, "E114.MirrorCS", {"start": v(-17.46, -5.56) * mm, "end": v(-20.64, -5.56) * mm});
            skArc(sketch, "E115.MirrorCS", {"start": v(1.59, -5.56) * mm, "mid": v(2.15, -5.79) * mm, "end": v(2.38, -6.35) * mm});
            skPoint(sketch, "E116.MirrorP", {"position": v(26.99, -20.64) * mm});
            skPoint(sketch, "E117.MirrorP", {"position": v(-19.05, -12.7) * mm});
            skLineSegment(sketch, "E118.MirrorCS", {"start": v(-20.64, -26.2) * mm, "end": v(-20.64, -24.6) * mm});
            skPoint(sketch, "E119.MirrorP", {"position": v(0, -25.4) * mm});
            skArc(sketch, "E120.MirrorCS", {"start": v(6.35, -10.32) * mm, "mid": v(6.91, -10.55) * mm, "end": v(7.14, -11.11) * mm});
            skPoint(sketch, "E121.MirrorP", {"position": v(14.29, -20.64) * mm});
            skLineSegment(sketch, "E122.MirrorCS", {"start": v(-24.6, -20.64) * mm, "end": v(-26.2, -20.64) * mm});
            skPoint(sketch, "E123.MirrorP", {"position": v(11.11, -20.64) * mm});
            skArc(sketch, "E124.MirrorCS", {"start": v(-4.76, -24.6) * mm, "mid": v(-4.53, -24.04) * mm, "end": v(-3.97, -23.81) * mm});
            skLineSegment(sketch, "E125.MirrorCS", {"start": v(-4.76, -26.2) * mm, "end": v(-4.76, -24.6) * mm});
            skLineSegment(sketch, "E126.MirrorCS", {"start": v(-17.46, -26.2) * mm, "end": v(-17.46, -24.6) * mm});
            skArc(sketch, "E127.MirrorCS", {"start": v(-1.59, -21.43) * mm, "mid": v(-1.36, -20.87) * mm, "end": v(-0.8, -20.64) * mm});
            skPoint(sketch, "E128.MirrorP", {"position": v(23.81, -20.64) * mm});
            skArc(sketch, "E129.MirrorCS", {"start": v(-19.69, 2.38) * mm, "mid": v(-19.45, 2.94) * mm, "end": v(-18.9, 3.17) * mm});
            skArc(sketch, "E130.MirrorCS", {"start": v(-24.6, -20.64) * mm, "mid": v(-24.04, -20.87) * mm, "end": v(-23.81, -21.43) * mm});
            skPoint(sketch, "E131.MirrorP", {"position": v(0, -12.7) * mm});
            skArc(sketch, "E132.MirrorCS", {"start": v(-21.43, -23.81) * mm, "mid": v(-20.87, -24.04) * mm, "end": v(-20.64, -24.6) * mm});
            skPoint(sketch, "E133.MirrorP", {"position": v(25.4, -25.4) * mm});
            skPoint(sketch, "E134.MirrorP", {"position": v(-12.7, -25.4) * mm});
            skLineSegment(sketch, "E135.MirrorCS", {"start": v(-7.94, -26.2) * mm, "end": v(-7.94, -24.6) * mm});
            skPoint(sketch, "E136.MirrorP", {"position": v(19.05, -12.7) * mm});
            skArc(sketch, "E137.MirrorCS", {"start": v(7.75, -9.52) * mm, "mid": v(7.2, -9.3) * mm, "end": v(6.96, -8.73) * mm});
            skLineSegment(sketch, "E138.MirrorCS", {"start": v(-11.11, -29.37) * mm, "end": v(-11.11, -21.43) * mm});
            skArc(sketch, "E139.MirrorCS", {"start": v(17.46, -19.84) * mm, "mid": v(16.9, -19.61) * mm, "end": v(16.67, -19.05) * mm});
            skPoint(sketch, "E140.MirrorP", {"position": v(4.76, -23.81) * mm});
            skPoint(sketch, "E141.MirrorP", {"position": v(-23.81, -30.16) * mm});
            skLineSegment(sketch, "E142.MirrorCS", {"start": v(-6.99, -8.73) * mm, "end": v(-6.99, 8.73) * mm});
            skLineSegment(sketch, "E143.MirrorCS", {"start": v(25.4, -15.08) * mm, "end": v(12.7, -15.08) * mm});
            skPoint(sketch, "E144.MirrorP", {"position": v(-7.14, -10.32) * mm});
            skLineSegment(sketch, "E145.MirrorCS", {"start": v(6.96, -8.73) * mm, "end": v(6.96, 8.73) * mm});
            skLineSegment(sketch, "E146.MirrorCS", {"start": v(0.6, -2.38) * mm, "end": v(0.6, 2.38) * mm});
            skLineSegment(sketch, "E147.MirrorCS", {"start": v(29.37, -23.81) * mm, "end": v(21.43, -23.81) * mm});
            skPoint(sketch, "E148.MirrorP", {"position": v(7.14, -10.32) * mm});
            skPoint(sketch, "E149.MirrorP", {"position": v(-11.11, -30.16) * mm});
            skLineSegment(sketch, "E150.MirrorCS", {"start": v(-7.14, -14.29) * mm, "end": v(-7.14, -11.11) * mm});
            skLineSegment(sketch, "E151.MirrorCS", {"start": v(16.67, -26.99) * mm, "end": v(8.73, -26.99) * mm});
            skPoint(sketch, "E152.MirrorP", {"position": v(-16.67, -5.56) * mm});
            skPoint(sketch, "E153.MirrorP", {"position": v(-26.99, -20.64) * mm});
            skLineSegment(sketch, "E154.MirrorCS", {"start": v(13.5, -30.16) * mm, "end": v(11.9, -30.16) * mm});
            skLineSegment(sketch, "E155.MirrorCS", {"start": v(20.64, -19.84) * mm, "end": v(17.46, -19.84) * mm});
            skLineSegment(sketch, "E156.MirrorCS", {"start": v(26.2, -14.29) * mm, "end": v(26.2, -11.11) * mm});
            skLineSegment(sketch, "E157.MirrorCS", {"start": v(-12.7, -10.32) * mm, "end": v(-25.4, -10.32) * mm});
            skLineSegment(sketch, "E158.MirrorCS", {"start": v(-26.99, -20.64) * mm, "end": v(-14.29, -20.64) * mm, "construction": true});
            skArc(sketch, "E159.MirrorCS", {"start": v(18.87, 3.18) * mm, "mid": v(19.43, 2.94) * mm, "end": v(19.66, 2.38) * mm});
            skPoint(sketch, "E160.MirrorP", {"position": v(7.14, -15.08) * mm});
            skLineSegment(sketch, "E161.MirrorCS", {"start": v(-1.59, -29.37) * mm, "end": v(-1.59, -21.43) * mm});
            skPoint(sketch, "E162.MirrorP", {"position": v(1.59, -30.16) * mm});
            skLineSegment(sketch, "E163.MirrorCS", {"start": v(16.67, -23.81) * mm, "end": v(8.73, -23.81) * mm});
            skPoint(sketch, "E164.MirrorP", {"position": v(-23.81, -20.64) * mm});
            skLineSegment(sketch, "E165.MirrorCS", {"start": v(-8.73, -26.99) * mm, "end": v(-16.67, -26.99) * mm});
            skPoint(sketch, "E166.MirrorP", {"position": v(26.99, -30.16) * mm});
            skLineSegment(sketch, "E167.MirrorCS", {"start": v(19.66, -2.38) * mm, "end": v(19.66, 2.38) * mm});
            skLineSegment(sketch, "E168.MirrorCS", {"start": v(-14.29, -29.37) * mm, "end": v(-14.29, -21.43) * mm});
            skPoint(sketch, "E169.MirrorP", {"position": v(26.2, -15.08) * mm});
            skLineSegment(sketch, "E170.MirrorCS", {"start": v(18.87, -3.17) * mm, "end": v(1.4, -3.18) * mm});
            skPoint(sketch, "E171.MirrorP", {"position": v(11.9, -15.08) * mm});
            skPoint(sketch, "E172.MirrorP", {"position": v(7.94, -23.81) * mm});
            skPoint(sketch, "E173.MirrorP", {"position": v(-26.2, -15.08) * mm});
            skPoint(sketch, "E174.MirrorP", {"position": v(30.16, -26.99) * mm});
            skLineSegment(sketch, "E175.MirrorCS", {"start": v(29.37, -26.99) * mm, "end": v(21.43, -26.99) * mm});
            skLineSegment(sketch, "E176.MirrorCS", {"start": v(-8.73, -23.81) * mm, "end": v(-16.67, -23.81) * mm});
            skLineSegment(sketch, "E177.MirrorCS", {"start": v(3.97, -23.81) * mm, "end": v(-3.97, -23.81) * mm});
            skArc(sketch, "E178.MirrorCS", {"start": v(2.38, -19.05) * mm, "mid": v(2.15, -19.61) * mm, "end": v(1.59, -19.84) * mm});
            skPoint(sketch, "E179.MirrorP", {"position": v(-19.69, 3.17) * mm});
            skLineSegment(sketch, "E180.MirrorCS", {"start": v(17.46, -26.2) * mm, "end": v(17.46, -24.6) * mm});
            skLineSegment(sketch, "E181.MirrorCS", {"start": v(30.16, -26.2) * mm, "end": v(30.16, -24.6) * mm});
            skLineSegment(sketch, "E182.MirrorCS", {"start": v(2.38, -19.05) * mm, "end": v(2.38, -6.35) * mm});
            skLineSegment(sketch, "E183.MirrorCS", {"start": v(0, -25.4) * mm, "end": v(-25.4, -25.4) * mm, "construction": true});
            skLineSegment(sketch, "E184.MirrorCS", {"start": v(23.81, -29.37) * mm, "end": v(23.81, -21.43) * mm});
            skLineSegment(sketch, "E185.MirrorCS", {"start": v(0, 0) * mm, "end": v(0, -25.4) * mm, "construction": true});
            skLineSegment(sketch, "E186.MirrorCS", {"start": v(0, 0) * mm, "end": v(0, -12.7) * mm, "construction": true});
            skLineSegment(sketch, "E187.MirrorCS", {"start": v(6.35, -15.08) * mm, "end": v(-6.35, -15.08) * mm});
            skPoint(sketch, "E188.MirrorP", {"position": v(-26.99, -30.16) * mm});
            skLineSegment(sketch, "E189.MirrorCS", {"start": v(4.76, -26.2) * mm, "end": v(4.76, -24.6) * mm});
            skLineSegment(sketch, "E190.MirrorCS", {"start": v(-30.16, -26.2) * mm, "end": v(-30.16, -24.6) * mm});
            skLineSegment(sketch, "E191.MirrorCS", {"start": v(-21.43, -26.99) * mm, "end": v(-29.37, -26.99) * mm});
            skPoint(sketch, "E192.MirrorP", {"position": v(-30.16, -26.99) * mm});
            skPoint(sketch, "E193.MirrorP", {"position": v(-26.2, -10.32) * mm});
            skPoint(sketch, "E194.MirrorP", {"position": v(-7.94, -26.99) * mm});
            skPoint(sketch, "E195.MirrorP", {"position": v(-4.76, -23.81) * mm});
            skLineSegment(sketch, "E196.MirrorCS", {"start": v(7.94, -26.2) * mm, "end": v(7.94, -24.6) * mm});
            skLineSegment(sketch, "E197.MirrorCS", {"start": v(21.43, -19.05) * mm, "end": v(21.43, -6.35) * mm});
            skLineSegment(sketch, "E198.MirrorCS", {"start": v(20.64, -26.2) * mm, "end": v(20.64, -24.6) * mm});
            skLineSegment(sketch, "E199.MirrorCS", {"start": v(-26.99, -29.37) * mm, "end": v(-26.99, -21.43) * mm});
            skLineSegment(sketch, "E200.MirrorCS", {"start": v(-23.81, -29.37) * mm, "end": v(-23.81, -21.43) * mm});
            skPoint(sketch, "E201.MirrorP", {"position": v(16.67, -5.56) * mm});
            skLineSegment(sketch, "E202.MirrorCS", {"start": v(-21.43, -23.81) * mm, "end": v(-29.37, -23.81) * mm});
            skPoint(sketch, "E203.MirrorP", {"position": v(2.38, -5.56) * mm});
            skPoint(sketch, "E204.MirrorP", {"position": v(-7.94, -23.81) * mm});
            skPoint(sketch, "E205.MirrorP", {"position": v(-1.59, -30.16) * mm});
            skLineSegment(sketch, "E206.MirrorCS", {"start": v(25.4, -10.32) * mm, "end": v(12.7, -10.32) * mm});
            skLineSegment(sketch, "E207.MirrorCS", {"start": v(-12.54, 9.53) * mm, "end": v(7.75, 9.53) * mm, "construction": true});
            skPoint(sketch, "E208.MirrorP", {"position": v(20.64, -26.99) * mm});
            skPoint(sketch, "E209.MirrorP", {"position": v(-4.76, -26.99) * mm});
            skLineSegment(sketch, "E210.MirrorCS", {"start": v(11.9, -14.29) * mm, "end": v(11.9, -11.11) * mm});
            skPoint(sketch, "E211.MirrorP", {"position": v(-0.64, 3.18) * mm});
            skPoint(sketch, "E212.MirrorP", {"position": v(-11.11, -20.64) * mm});
            skPoint(sketch, "E213.MirrorP", {"position": v(11.11, -30.16) * mm});
            skLineSegment(sketch, "E214.MirrorCS", {"start": v(-1.43, 3.18) * mm, "end": v(-18.9, 3.17) * mm});
            skPoint(sketch, "E215.MirrorP", {"position": v(-17.46, -23.81) * mm});
            skLineSegment(sketch, "E216.MirrorCS", {"start": v(13.3, -8.73) * mm, "end": v(13.3, 8.73) * mm});
            skLineSegment(sketch, "E217.MirrorCS", {"start": v(-1.43, -3.17) * mm, "end": v(-18.9, -3.18) * mm});
            skLineSegment(sketch, "E218.MirrorCS", {"start": v(-12.7, -15.08) * mm, "end": v(-25.4, -15.08) * mm});
            skPoint(sketch, "E219.MirrorP", {"position": v(-30.16, -23.81) * mm});
            skPoint(sketch, "E220.MirrorP", {"position": v(-0.64, -3.17) * mm});
            skLineSegment(sketch, "E221.MirrorCS", {"start": v(6.35, -10.32) * mm, "end": v(-6.35, -10.32) * mm});
            skLineSegment(sketch, "E222.MirrorCS", {"start": v(-19.69, -2.38) * mm, "end": v(-19.69, 2.38) * mm});
            skPoint(sketch, "E223.MirrorP", {"position": v(-7.14, -15.08) * mm});
            skLineSegment(sketch, "E224.MirrorCS", {"start": v(-21.43, -19.05) * mm, "end": v(-21.43, -6.35) * mm});
            skPoint(sketch, "E225.MirrorP", {"position": v(7.94, -26.99) * mm});
            skLineSegment(sketch, "E226.MirrorCS", {"start": v(-11.9, -14.29) * mm, "end": v(-11.9, -11.11) * mm});
            skPoint(sketch, "E227.MirrorP", {"position": v(4.76, -26.99) * mm});
            skPoint(sketch, "E228.MirrorP", {"position": v(-14.29, -30.16) * mm});
            skLineSegment(sketch, "E229.MirrorCS", {"start": v(26.2, -20.64) * mm, "end": v(24.6, -20.64) * mm});
            skLineSegment(sketch, "E230.MirrorCS", {"start": v(13.5, -20.64) * mm, "end": v(11.9, -20.64) * mm});
            skPoint(sketch, "E231.MirrorP", {"position": v(-2.38, -5.56) * mm});
            skLineSegment(sketch, "E232.MirrorCS", {"start": v(3.97, -26.99) * mm, "end": v(-3.97, -26.99) * mm});
            skLineSegment(sketch, "E233.MirrorCS", {"start": v(-24.6, -30.16) * mm, "end": v(-26.2, -30.16) * mm});
            skArc(sketch, "E234.MirrorCS", {"start": v(19.66, -2.38) * mm, "mid": v(19.43, -2.94) * mm, "end": v(18.87, -3.17) * mm});
            skLineSegment(sketch, "E235.MirrorCS", {"start": v(20.64, -5.56) * mm, "end": v(17.46, -5.56) * mm});
            skLineSegment(sketch, "E236.MirrorCS", {"start": v(0, -12.7) * mm, "end": v(-19.05, -12.7) * mm, "construction": true});
            skLineSegment(sketch, "E237.MirrorCS", {"start": v(-21.43, -5.56) * mm, "end": v(-2.38, -5.56) * mm, "construction": true});
            skPoint(sketch, "E238.MirrorP", {"position": v(1.59, -20.64) * mm});
            skPoint(sketch, "E239.MirrorP", {"position": v(4.76, -20.64) * mm});
            skLineSegment(sketch, "E240.MirrorCS", {"start": v(1.59, -5.56) * mm, "end": v(-1.59, -5.56) * mm});
            skPoint(sketch, "E241.MirrorP", {"position": v(-17.46, -26.99) * mm});
            skLineSegment(sketch, "E242.MirrorCS", {"start": v(-0.64, -2.38) * mm, "end": v(-0.64, 2.38) * mm});
            skPoint(sketch, "E243.MirrorP", {"position": v(26.2, -10.32) * mm});
            skPoint(sketch, "E244.MirrorP", {"position": v(14.29, -30.16) * mm});
            skLineSegment(sketch, "E245.MirrorCS", {"start": v(-17.46, -19.84) * mm, "end": v(-20.64, -19.84) * mm});
            skPoint(sketch, "E246.MirrorP", {"position": v(23.81, -30.16) * mm});
            skPoint(sketch, "E247.MirrorP", {"position": v(17.46, -26.99) * mm});
            skPoint(sketch, "E248.MirrorP", {"position": v(-21.43, -5.56) * mm});
            skLineSegment(sketch, "E249.MirrorCS", {"start": v(-11.9, -20.64) * mm, "end": v(-13.5, -20.64) * mm});
            skPoint(sketch, "E250.MirrorP", {"position": v(-1.59, -20.64) * mm});
            skLineSegment(sketch, "E251.MirrorCS", {"start": v(16.67, -19.05) * mm, "end": v(16.67, -6.35) * mm});
            skPoint(sketch, "E252.MirrorP", {"position": v(-16.67, -19.84) * mm});
            skPoint(sketch, "E253.MirrorP", {"position": v(-11.9, -15.08) * mm});
            skLineSegment(sketch, "E254.MirrorCS", {"start": v(18.87, 3.18) * mm, "end": v(1.4, 3.17) * mm});
            skPoint(sketch, "E255.MirrorP", {"position": v(-4.76, -20.64) * mm});
            skLineSegment(sketch, "E256.MirrorCS", {"start": v(1.59, -19.84) * mm, "end": v(-1.59, -19.84) * mm});
            skLineSegment(sketch, "E257.MirrorCS", {"start": v(14.29, -29.37) * mm, "end": v(14.29, -21.43) * mm});
            skLineSegment(sketch, "E258.MirrorCS", {"start": v(26.2, -30.16) * mm, "end": v(24.6, -30.16) * mm});
            skLineSegment(sketch, "E259.MirrorCS", {"start": v(11.11, -29.37) * mm, "end": v(11.11, -21.43) * mm});
            skPoint(sketch, "E260.MirrorP", {"position": v(21.43, -5.56) * mm});
            skPoint(sketch, "E261.MirrorP", {"position": v(-20.64, -26.99) * mm});
            skPoint(sketch, "E262.MirrorP", {"position": v(-20.64, -23.81) * mm});
            skLineSegment(sketch, "E263.MirrorCS", {"start": v(0.8, -30.16) * mm, "end": v(-0.8, -30.16) * mm});
            skLineSegment(sketch, "E264.MirrorCS", {"start": v(-2.38, -19.05) * mm, "end": v(-2.38, -6.35) * mm});
            skPoint(sketch, "E265.MirrorP", {"position": v(-11.9, -10.32) * mm});
            skLineSegment(sketch, "E266.MirrorCS", {"start": v(-11.9, -30.16) * mm, "end": v(-13.5, -30.16) * mm});
            skPoint(sketch, "E267.MirrorP", {"position": v(-7.94, -20.64) * mm});
            skLineSegment(sketch, "E268.MirrorCS", {"start": v(26.99, -29.37) * mm, "end": v(26.99, -21.43) * mm});
            skPoint(sketch, "E269.MirrorP", {"position": v(17.46, -23.81) * mm});
            skPoint(sketch, "E270.MirrorP", {"position": v(11.9, -10.32) * mm});
            skPoint(sketch, "E271.MirrorP", {"position": v(-14.29, -20.64) * mm});
            skLineSegment(sketch, "E272.MirrorCS", {"start": v(-13.34, -8.73) * mm, "end": v(-13.34, 8.73) * mm});
            skPoint(sketch, "E273.MirrorP", {"position": v(-19.69, -3.18) * mm});
            skPoint(sketch, "E274.MirrorP", {"position": v(-21.43, -19.84) * mm});
            skLineSegment(sketch, "E275.MirrorCS", {"start": v(1.59, -29.37) * mm, "end": v(1.59, -21.43) * mm});
            skPoint(sketch, "E276.MirrorP", {"position": v(30.16, -23.81) * mm});
            skLineSegment(sketch, "E277.MirrorCS", {"start": v(-16.67, -19.05) * mm, "end": v(-16.67, -6.35) * mm});
            skLineSegment(sketch, "E278.MirrorCS", {"start": v(7.14, -14.29) * mm, "end": v(7.14, -11.11) * mm});
            skLineSegment(sketch, "E279.MirrorCS", {"start": v(-26.2, -14.29) * mm, "end": v(-26.2, -11.11) * mm});
            skPoint(sketch, "E280.MirrorP", {"position": v(20.64, -23.81) * mm});
            skPoint(sketch, "E281.MirrorP", {"position": v(7.94, -20.64) * mm});
            skSolve(sketch);
        }
        {
            var Q0;
            Q0 = qSketchRegion(id + "F2", true);
            extrude(context, id + "F3", {"entities" : qUnion([Q0]), "operationType" : NewBodyOperationType.REMOVE, "oppositeDirection" : true, "depth" : 3.17 * mm, "offsetDistance" : 25.4 * mm});
        }
        {
            var Q0;
            Q0=makeQuery(id+"F3.boolean.opBoolean","COPY",FACE,{"derivedFrom":makeQuery(id+"F3.opExtrude","CAP_FACE",FACE,{"disambiguationData":[OSD([sQuery(id+"F2.wireOp",EDGE,"E10.bottom"),sQuery(id+"F2.wireOp",EDGE,"E10.top"),sQuery(id+"F2.wireOp",EDGE,"E10.left"),sQuery(id+"F2.wireOp",EDGE,"E10.right"),sQuery(id+"F2.wireOp",EDGE,"E11.bottom"),sQuery(id+"F2.wireOp",EDGE,"E11.top"),sQuery(id+"F2.wireOp",EDGE,"E11.left"),sQuery(id+"F2.wireOp",EDGE,"E11.right"),sQuery(id+"F2.wireOp",EDGE,"E12.filletArc"),sQuery(id+"F2.wireOp",EDGE,"E13.filletArc"),sQuery(id+"F2.wireOp",EDGE,"E14.filletArc"),sQuery(id+"F2.wireOp",EDGE,"E15.filletArc"),sQuery(id+"F2.wireOp",EDGE,"E16.filletArc"),sQuery(id+"F2.wireOp",EDGE,"E17.filletArc"),sQuery(id+"F2.wireOp",EDGE,"E18.filletArc"),sQuery(id+"F2.wireOp",EDGE,"E19.filletArc")])],"isStart":false})});
            var Q1;
            Q1=makeQuery(id+"F3.boolean.opBoolean","COPY",FACE,{"derivedFrom":makeQuery(id+"F3.opExtrude","CAP_FACE",FACE,{"disambiguationData":[OSD([sQuery(id+"F2.wireOp",EDGE,"E40.1.0.1"),sQuery(id+"F2.wireOp",EDGE,"E40.1.0.2"),sQuery(id+"F2.wireOp",EDGE,"E40.1.0.9"),sQuery(id+"F2.wireOp",EDGE,"E40.1.0.10"),sQuery(id+"F2.wireOp",EDGE,"E40.1.0.11"),sQuery(id+"F2.wireOp",EDGE,"E40.1.0.12"),sQuery(id+"F2.wireOp",EDGE,"E40.1.0.15"),sQuery(id+"F2.wireOp",EDGE,"E40.1.0.16"),sQuery(id+"F2.wireOp",EDGE,"E40.1.0.18"),sQuery(id+"F2.wireOp",EDGE,"E40.1.0.19"),sQuery(id+"F2.wireOp",EDGE,"E40.1.0.20"),sQuery(id+"F2.wireOp",EDGE,"E40.1.0.21"),sQuery(id+"F2.wireOp",EDGE,"E40.1.0.22"),sQuery(id+"F2.wireOp",EDGE,"E40.1.0.23"),sQuery(id+"F2.wireOp",EDGE,"E40.1.0.24"),sQuery(id+"F2.wireOp",EDGE,"E40.1.0.25")])],"isStart":false})});
            var Q2;
            Q2=makeQuery(id+"F3.boolean.opBoolean","COPY",FACE,{"derivedFrom":makeQuery(id+"F3.opExtrude","CAP_FACE",FACE,{"disambiguationData":[OSD([sQuery(id+"F2.wireOp",EDGE,"E40.2.0.1"),sQuery(id+"F2.wireOp",EDGE,"E40.2.0.2"),sQuery(id+"F2.wireOp",EDGE,"E40.2.0.9"),sQuery(id+"F2.wireOp",EDGE,"E40.2.0.10"),sQuery(id+"F2.wireOp",EDGE,"E40.2.0.11"),sQuery(id+"F2.wireOp",EDGE,"E40.2.0.12"),sQuery(id+"F2.wireOp",EDGE,"E40.2.0.15"),sQuery(id+"F2.wireOp",EDGE,"E40.2.0.16"),sQuery(id+"F2.wireOp",EDGE,"E40.2.0.18"),sQuery(id+"F2.wireOp",EDGE,"E40.2.0.19"),sQuery(id+"F2.wireOp",EDGE,"E40.2.0.20"),sQuery(id+"F2.wireOp",EDGE,"E40.2.0.21"),sQuery(id+"F2.wireOp",EDGE,"E40.2.0.22"),sQuery(id+"F2.wireOp",EDGE,"E40.2.0.23"),sQuery(id+"F2.wireOp",EDGE,"E40.2.0.24"),sQuery(id+"F2.wireOp",EDGE,"E40.2.0.25")])],"isStart":false})});
            var Q3;
            Q3=makeQuery(id+"F3.boolean.opBoolean","COPY",FACE,{"derivedFrom":makeQuery(id+"F3.opExtrude","CAP_FACE",FACE,{"disambiguationData":[OSD([sQuery(id+"F2.wireOp",EDGE,"E40.3.0.1"),sQuery(id+"F2.wireOp",EDGE,"E40.3.0.2"),sQuery(id+"F2.wireOp",EDGE,"E40.3.0.9"),sQuery(id+"F2.wireOp",EDGE,"E40.3.0.10"),sQuery(id+"F2.wireOp",EDGE,"E40.3.0.11"),sQuery(id+"F2.wireOp",EDGE,"E40.3.0.12"),sQuery(id+"F2.wireOp",EDGE,"E40.3.0.15"),sQuery(id+"F2.wireOp",EDGE,"E40.3.0.16"),sQuery(id+"F2.wireOp",EDGE,"E40.3.0.18"),sQuery(id+"F2.wireOp",EDGE,"E40.3.0.19"),sQuery(id+"F2.wireOp",EDGE,"E40.3.0.20"),sQuery(id+"F2.wireOp",EDGE,"E40.3.0.21"),sQuery(id+"F2.wireOp",EDGE,"E40.3.0.22"),sQuery(id+"F2.wireOp",EDGE,"E40.3.0.23"),sQuery(id+"F2.wireOp",EDGE,"E40.3.0.24"),sQuery(id+"F2.wireOp",EDGE,"E40.3.0.25")])],"isStart":false})});
            var Q4;
            Q4=makeQuery(id+"F3.boolean.opBoolean","COPY",FACE,{"derivedFrom":makeQuery(id+"F3.opExtrude","CAP_FACE",FACE,{"disambiguationData":[OSD([sQuery(id+"F2.wireOp",EDGE,"E40.4.0.1"),sQuery(id+"F2.wireOp",EDGE,"E40.4.0.2"),sQuery(id+"F2.wireOp",EDGE,"E40.4.0.9"),sQuery(id+"F2.wireOp",EDGE,"E40.4.0.10"),sQuery(id+"F2.wireOp",EDGE,"E40.4.0.11"),sQuery(id+"F2.wireOp",EDGE,"E40.4.0.12"),sQuery(id+"F2.wireOp",EDGE,"E40.4.0.15"),sQuery(id+"F2.wireOp",EDGE,"E40.4.0.16"),sQuery(id+"F2.wireOp",EDGE,"E40.4.0.18"),sQuery(id+"F2.wireOp",EDGE,"E40.4.0.19"),sQuery(id+"F2.wireOp",EDGE,"E40.4.0.20"),sQuery(id+"F2.wireOp",EDGE,"E40.4.0.21"),sQuery(id+"F2.wireOp",EDGE,"E40.4.0.22"),sQuery(id+"F2.wireOp",EDGE,"E40.4.0.23"),sQuery(id+"F2.wireOp",EDGE,"E40.4.0.24"),sQuery(id+"F2.wireOp",EDGE,"E40.4.0.25")])],"isStart":false})});
            var Q5;
            Q5=makeQuery(id+"F3.boolean.opBoolean","COPY",FACE,{"derivedFrom":makeQuery(id+"F3.opExtrude","CAP_FACE",FACE,{"disambiguationData":[OSD([sQuery(id+"F2.wireOp",EDGE,"E41.2.0.1"),sQuery(id+"F2.wireOp",EDGE,"E41.2.0.2"),sQuery(id+"F2.wireOp",EDGE,"E41.2.0.7"),sQuery(id+"F2.wireOp",EDGE,"E41.2.0.9"),sQuery(id+"F2.wireOp",EDGE,"E41.2.0.10"),sQuery(id+"F2.wireOp",EDGE,"E41.2.0.11"),sQuery(id+"F2.wireOp",EDGE,"E41.2.0.16"),sQuery(id+"F2.wireOp",EDGE,"E41.2.0.18"),sQuery(id+"F2.wireOp",EDGE,"E41.2.0.19"),sQuery(id+"F2.wireOp",EDGE,"E41.2.0.20"),sQuery(id+"F2.wireOp",EDGE,"E41.2.0.22"),sQuery(id+"F2.wireOp",EDGE,"E41.2.0.23"),sQuery(id+"F2.wireOp",EDGE,"E41.2.0.24"),sQuery(id+"F2.wireOp",EDGE,"E41.2.0.25"),sQuery(id+"F2.wireOp",EDGE,"E41.2.0.26"),sQuery(id+"F2.wireOp",EDGE,"E41.2.0.27")])],"isStart":false})});
            var Q6;
            Q6=makeQuery(id+"F3.boolean.opBoolean","COPY",FACE,{"derivedFrom":makeQuery(id+"F3.opExtrude","CAP_FACE",FACE,{"disambiguationData":[OSD([sQuery(id+"F2.wireOp",EDGE,"E41.1.0.1"),sQuery(id+"F2.wireOp",EDGE,"E41.1.0.2"),sQuery(id+"F2.wireOp",EDGE,"E41.1.0.7"),sQuery(id+"F2.wireOp",EDGE,"E41.1.0.9"),sQuery(id+"F2.wireOp",EDGE,"E41.1.0.10"),sQuery(id+"F2.wireOp",EDGE,"E41.1.0.11"),sQuery(id+"F2.wireOp",EDGE,"E41.1.0.16"),sQuery(id+"F2.wireOp",EDGE,"E41.1.0.18"),sQuery(id+"F2.wireOp",EDGE,"E41.1.0.19"),sQuery(id+"F2.wireOp",EDGE,"E41.1.0.20"),sQuery(id+"F2.wireOp",EDGE,"E41.1.0.22"),sQuery(id+"F2.wireOp",EDGE,"E41.1.0.23"),sQuery(id+"F2.wireOp",EDGE,"E41.1.0.24"),sQuery(id+"F2.wireOp",EDGE,"E41.1.0.25"),sQuery(id+"F2.wireOp",EDGE,"E41.1.0.26"),sQuery(id+"F2.wireOp",EDGE,"E41.1.0.27")])],"isStart":false})});
            var Q7;
            Q7=makeQuery(id+"F3.boolean.opBoolean","COPY",FACE,{"derivedFrom":makeQuery(id+"F3.opExtrude","CAP_FACE",FACE,{"disambiguationData":[OSD([sQuery(id+"F2.wireOp",EDGE,"E20.bottom"),sQuery(id+"F2.wireOp",EDGE,"E20.top"),sQuery(id+"F2.wireOp",EDGE,"E20.left"),sQuery(id+"F2.wireOp",EDGE,"E20.right"),sQuery(id+"F2.wireOp",EDGE,"E21.bottom"),sQuery(id+"F2.wireOp",EDGE,"E21.top"),sQuery(id+"F2.wireOp",EDGE,"E21.left"),sQuery(id+"F2.wireOp",EDGE,"E21.right"),sQuery(id+"F2.wireOp",EDGE,"E22.filletArc"),sQuery(id+"F2.wireOp",EDGE,"E23.filletArc"),sQuery(id+"F2.wireOp",EDGE,"E24.filletArc"),sQuery(id+"F2.wireOp",EDGE,"E25.filletArc"),sQuery(id+"F2.wireOp",EDGE,"E26.filletArc"),sQuery(id+"F2.wireOp",EDGE,"E27.filletArc"),sQuery(id+"F2.wireOp",EDGE,"E28.filletArc"),sQuery(id+"F2.wireOp",EDGE,"E29.filletArc")])],"isStart":false})});
            var Q8;
            Q8=makeQuery(id+"F3.boolean.opBoolean","COPY",FACE,{"derivedFrom":makeQuery(id+"F3.opExtrude","CAP_FACE",FACE,{"disambiguationData":[OSD([sQuery(id+"F2.wireOp",EDGE,"E30.bottom"),sQuery(id+"F2.wireOp",EDGE,"E30.top"),sQuery(id+"F2.wireOp",EDGE,"E30.left"),sQuery(id+"F2.wireOp",EDGE,"E30.right"),sQuery(id+"F2.wireOp",EDGE,"E31.bottom"),sQuery(id+"F2.wireOp",EDGE,"E31.top"),sQuery(id+"F2.wireOp",EDGE,"E31.left"),sQuery(id+"F2.wireOp",EDGE,"E31.right"),sQuery(id+"F2.wireOp",EDGE,"E32.filletArc"),sQuery(id+"F2.wireOp",EDGE,"E33.filletArc"),sQuery(id+"F2.wireOp",EDGE,"E34.filletArc"),sQuery(id+"F2.wireOp",EDGE,"E35.filletArc"),sQuery(id+"F2.wireOp",EDGE,"E36.filletArc"),sQuery(id+"F2.wireOp",EDGE,"E37.filletArc"),sQuery(id+"F2.wireOp",EDGE,"E38.filletArc"),sQuery(id+"F2.wireOp",EDGE,"E39.filletArc")])],"isStart":false})});
            var Q9;
            Q9=makeQuery(id+"F3.boolean.opBoolean","COPY",FACE,{"derivedFrom":makeQuery(id+"F3.opExtrude","CAP_FACE",FACE,{"disambiguationData":[OSD([sQuery(id+"F2.wireOp",EDGE,"E42.1.0.0"),sQuery(id+"F2.wireOp",EDGE,"E42.1.0.1"),sQuery(id+"F2.wireOp",EDGE,"E42.1.0.2"),sQuery(id+"F2.wireOp",EDGE,"E42.1.0.3"),sQuery(id+"F2.wireOp",EDGE,"E42.1.0.4"),sQuery(id+"F2.wireOp",EDGE,"E42.1.0.5"),sQuery(id+"F2.wireOp",EDGE,"E42.1.0.6"),sQuery(id+"F2.wireOp",EDGE,"E42.1.0.7"),sQuery(id+"F2.wireOp",EDGE,"E42.1.0.8"),sQuery(id+"F2.wireOp",EDGE,"E42.1.0.9"),sQuery(id+"F2.wireOp",EDGE,"E42.1.0.10"),sQuery(id+"F2.wireOp",EDGE,"E42.1.0.11"),sQuery(id+"F2.wireOp",EDGE,"E42.1.0.12"),sQuery(id+"F2.wireOp",EDGE,"E42.1.0.13"),sQuery(id+"F2.wireOp",EDGE,"E42.1.0.14"),sQuery(id+"F2.wireOp",EDGE,"E42.1.0.15")])],"isStart":false})});
            var Q10;
            Q10=makeQuery(id+"F3.boolean.opBoolean","COPY",FACE,{"derivedFrom":makeQuery(id+"F3.opExtrude","CAP_FACE",FACE,{"disambiguationData":[OSD([sQuery(id+"F2.wireOp",EDGE,"E44.MirrorCS"),sQuery(id+"F2.wireOp",EDGE,"E49.MirrorCS"),sQuery(id+"F2.wireOp",EDGE,"E60.MirrorCS"),sQuery(id+"F2.wireOp",EDGE,"E62.MirrorCS"),sQuery(id+"F2.wireOp",EDGE,"E63.MirrorCS"),sQuery(id+"F2.wireOp",EDGE,"E74.MirrorCS"),sQuery(id+"F2.wireOp",EDGE,"E83.MirrorCS"),sQuery(id+"F2.wireOp",EDGE,"E95.MirrorCS"),sQuery(id+"F2.wireOp",EDGE,"E114.MirrorCS"),sQuery(id+"F2.wireOp",EDGE,"E157.MirrorCS"),sQuery(id+"F2.wireOp",EDGE,"E218.MirrorCS"),sQuery(id+"F2.wireOp",EDGE,"E224.MirrorCS"),sQuery(id+"F2.wireOp",EDGE,"E226.MirrorCS"),sQuery(id+"F2.wireOp",EDGE,"E245.MirrorCS"),sQuery(id+"F2.wireOp",EDGE,"E277.MirrorCS"),sQuery(id+"F2.wireOp",EDGE,"E279.MirrorCS")])],"isStart":false})});
            var Q11;
            Q11=makeQuery(id+"F3.boolean.opBoolean","COPY",FACE,{"derivedFrom":makeQuery(id+"F3.opExtrude","CAP_FACE",FACE,{"disambiguationData":[OSD([sQuery(id+"F2.wireOp",EDGE,"E51.MirrorCS"),sQuery(id+"F2.wireOp",EDGE,"E53.MirrorCS"),sQuery(id+"F2.wireOp",EDGE,"E66.MirrorCS"),sQuery(id+"F2.wireOp",EDGE,"E89.MirrorCS"),sQuery(id+"F2.wireOp",EDGE,"E96.MirrorCS"),sQuery(id+"F2.wireOp",EDGE,"E115.MirrorCS"),sQuery(id+"F2.wireOp",EDGE,"E120.MirrorCS"),sQuery(id+"F2.wireOp",EDGE,"E150.MirrorCS"),sQuery(id+"F2.wireOp",EDGE,"E178.MirrorCS"),sQuery(id+"F2.wireOp",EDGE,"E182.MirrorCS"),sQuery(id+"F2.wireOp",EDGE,"E187.MirrorCS"),sQuery(id+"F2.wireOp",EDGE,"E221.MirrorCS"),sQuery(id+"F2.wireOp",EDGE,"E240.MirrorCS"),sQuery(id+"F2.wireOp",EDGE,"E256.MirrorCS"),sQuery(id+"F2.wireOp",EDGE,"E264.MirrorCS"),sQuery(id+"F2.wireOp",EDGE,"E278.MirrorCS")])],"isStart":false})});
            var Q12;
            Q12=makeQuery(id+"F3.boolean.opBoolean","COPY",FACE,{"derivedFrom":makeQuery(id+"F3.opExtrude","CAP_FACE",FACE,{"disambiguationData":[OSD([sQuery(id+"F2.wireOp",EDGE,"E75.MirrorCS"),sQuery(id+"F2.wireOp",EDGE,"E77.MirrorCS"),sQuery(id+"F2.wireOp",EDGE,"E84.MirrorCS"),sQuery(id+"F2.wireOp",EDGE,"E98.MirrorCS"),sQuery(id+"F2.wireOp",EDGE,"E101.MirrorCS"),sQuery(id+"F2.wireOp",EDGE,"E104.MirrorCS"),sQuery(id+"F2.wireOp",EDGE,"E108.MirrorCS"),sQuery(id+"F2.wireOp",EDGE,"E139.MirrorCS"),sQuery(id+"F2.wireOp",EDGE,"E143.MirrorCS"),sQuery(id+"F2.wireOp",EDGE,"E155.MirrorCS"),sQuery(id+"F2.wireOp",EDGE,"E156.MirrorCS"),sQuery(id+"F2.wireOp",EDGE,"E197.MirrorCS"),sQuery(id+"F2.wireOp",EDGE,"E206.MirrorCS"),sQuery(id+"F2.wireOp",EDGE,"E210.MirrorCS"),sQuery(id+"F2.wireOp",EDGE,"E235.MirrorCS"),sQuery(id+"F2.wireOp",EDGE,"E251.MirrorCS")])],"isStart":false})});
            var Q13;
            Q13=makeQuery(id+"F3.boolean.opBoolean","COPY",FACE,{"derivedFrom":makeQuery(id+"F3.opExtrude","CAP_FACE",FACE,{"disambiguationData":[OSD([sQuery(id+"F2.wireOp",EDGE,"E46.MirrorCS"),sQuery(id+"F2.wireOp",EDGE,"E54.MirrorCS"),sQuery(id+"F2.wireOp",EDGE,"E55.MirrorCS"),sQuery(id+"F2.wireOp",EDGE,"E65.MirrorCS"),sQuery(id+"F2.wireOp",EDGE,"E92.MirrorCS"),sQuery(id+"F2.wireOp",EDGE,"E100.MirrorCS"),sQuery(id+"F2.wireOp",EDGE,"E118.MirrorCS"),sQuery(id+"F2.wireOp",EDGE,"E122.MirrorCS"),sQuery(id+"F2.wireOp",EDGE,"E130.MirrorCS"),sQuery(id+"F2.wireOp",EDGE,"E132.MirrorCS"),sQuery(id+"F2.wireOp",EDGE,"E190.MirrorCS"),sQuery(id+"F2.wireOp",EDGE,"E191.MirrorCS"),sQuery(id+"F2.wireOp",EDGE,"E199.MirrorCS"),sQuery(id+"F2.wireOp",EDGE,"E200.MirrorCS"),sQuery(id+"F2.wireOp",EDGE,"E202.MirrorCS"),sQuery(id+"F2.wireOp",EDGE,"E233.MirrorCS")])],"isStart":false})});
            var Q14;
            Q14=makeQuery(id+"F3.boolean.opBoolean","COPY",FACE,{"derivedFrom":makeQuery(id+"F3.opExtrude","CAP_FACE",FACE,{"disambiguationData":[OSD([sQuery(id+"F2.wireOp",EDGE,"E47.MirrorCS"),sQuery(id+"F2.wireOp",EDGE,"E52.MirrorCS"),sQuery(id+"F2.wireOp",EDGE,"E61.MirrorCS"),sQuery(id+"F2.wireOp",EDGE,"E70.MirrorCS"),sQuery(id+"F2.wireOp",EDGE,"E79.MirrorCS"),sQuery(id+"F2.wireOp",EDGE,"E86.MirrorCS"),sQuery(id+"F2.wireOp",EDGE,"E90.MirrorCS"),sQuery(id+"F2.wireOp",EDGE,"E106.MirrorCS"),sQuery(id+"F2.wireOp",EDGE,"E126.MirrorCS"),sQuery(id+"F2.wireOp",EDGE,"E135.MirrorCS"),sQuery(id+"F2.wireOp",EDGE,"E138.MirrorCS"),sQuery(id+"F2.wireOp",EDGE,"E165.MirrorCS"),sQuery(id+"F2.wireOp",EDGE,"E168.MirrorCS"),sQuery(id+"F2.wireOp",EDGE,"E176.MirrorCS"),sQuery(id+"F2.wireOp",EDGE,"E249.MirrorCS"),sQuery(id+"F2.wireOp",EDGE,"E266.MirrorCS")])],"isStart":false})});
            var Q15;
            Q15=makeQuery(id+"F3.boolean.opBoolean","COPY",FACE,{"derivedFrom":makeQuery(id+"F3.opExtrude","CAP_FACE",FACE,{"disambiguationData":[OSD([sQuery(id+"F2.wireOp",EDGE,"E69.MirrorCS"),sQuery(id+"F2.wireOp",EDGE,"E78.MirrorCS"),sQuery(id+"F2.wireOp",EDGE,"E91.MirrorCS"),sQuery(id+"F2.wireOp",EDGE,"E93.MirrorCS"),sQuery(id+"F2.wireOp",EDGE,"E102.MirrorCS"),sQuery(id+"F2.wireOp",EDGE,"E105.MirrorCS"),sQuery(id+"F2.wireOp",EDGE,"E107.MirrorCS"),sQuery(id+"F2.wireOp",EDGE,"E124.MirrorCS"),sQuery(id+"F2.wireOp",EDGE,"E125.MirrorCS"),sQuery(id+"F2.wireOp",EDGE,"E127.MirrorCS"),sQuery(id+"F2.wireOp",EDGE,"E161.MirrorCS"),sQuery(id+"F2.wireOp",EDGE,"E177.MirrorCS"),sQuery(id+"F2.wireOp",EDGE,"E189.MirrorCS"),sQuery(id+"F2.wireOp",EDGE,"E232.MirrorCS"),sQuery(id+"F2.wireOp",EDGE,"E263.MirrorCS"),sQuery(id+"F2.wireOp",EDGE,"E275.MirrorCS")])],"isStart":false})});
            var Q16;
            Q16=makeQuery(id+"F3.boolean.opBoolean","COPY",FACE,{"derivedFrom":makeQuery(id+"F3.opExtrude","CAP_FACE",FACE,{"disambiguationData":[OSD([sQuery(id+"F2.wireOp",EDGE,"E56.MirrorCS"),sQuery(id+"F2.wireOp",EDGE,"E67.MirrorCS"),sQuery(id+"F2.wireOp",EDGE,"E68.MirrorCS"),sQuery(id+"F2.wireOp",EDGE,"E73.MirrorCS"),sQuery(id+"F2.wireOp",EDGE,"E76.MirrorCS"),sQuery(id+"F2.wireOp",EDGE,"E81.MirrorCS"),sQuery(id+"F2.wireOp",EDGE,"E82.MirrorCS"),sQuery(id+"F2.wireOp",EDGE,"E103.MirrorCS"),sQuery(id+"F2.wireOp",EDGE,"E151.MirrorCS"),sQuery(id+"F2.wireOp",EDGE,"E154.MirrorCS"),sQuery(id+"F2.wireOp",EDGE,"E163.MirrorCS"),sQuery(id+"F2.wireOp",EDGE,"E180.MirrorCS"),sQuery(id+"F2.wireOp",EDGE,"E196.MirrorCS"),sQuery(id+"F2.wireOp",EDGE,"E230.MirrorCS"),sQuery(id+"F2.wireOp",EDGE,"E257.MirrorCS"),sQuery(id+"F2.wireOp",EDGE,"E259.MirrorCS")])],"isStart":false})});
            var Q17;
            Q17=makeQuery(id+"F3.boolean.opBoolean","COPY",FACE,{"derivedFrom":makeQuery(id+"F3.opExtrude","CAP_FACE",FACE,{"disambiguationData":[OSD([sQuery(id+"F2.wireOp",EDGE,"E48.MirrorCS"),sQuery(id+"F2.wireOp",EDGE,"E59.MirrorCS"),sQuery(id+"F2.wireOp",EDGE,"E64.MirrorCS"),sQuery(id+"F2.wireOp",EDGE,"E71.MirrorCS"),sQuery(id+"F2.wireOp",EDGE,"E80.MirrorCS"),sQuery(id+"F2.wireOp",EDGE,"E88.MirrorCS"),sQuery(id+"F2.wireOp",EDGE,"E97.MirrorCS"),sQuery(id+"F2.wireOp",EDGE,"E109.MirrorCS"),sQuery(id+"F2.wireOp",EDGE,"E147.MirrorCS"),sQuery(id+"F2.wireOp",EDGE,"E175.MirrorCS"),sQuery(id+"F2.wireOp",EDGE,"E181.MirrorCS"),sQuery(id+"F2.wireOp",EDGE,"E184.MirrorCS"),sQuery(id+"F2.wireOp",EDGE,"E198.MirrorCS"),sQuery(id+"F2.wireOp",EDGE,"E229.MirrorCS"),sQuery(id+"F2.wireOp",EDGE,"E258.MirrorCS"),sQuery(id+"F2.wireOp",EDGE,"E268.MirrorCS")])],"isStart":false})});
            fillet(context, id + "F4", {"entities" : qUnion([Q0, Q1, Q2, Q3, Q4, Q5, Q6, Q7, Q8, Q9, Q10, Q11, Q12, Q13, Q14, Q15, Q16, Q17]), "tangentPropagation" : true, "radius" : 0.4 * mm, "defaultsChanged" : false, "vertexSettings" : [], "allowEdgeOverflow" : false});
        }
    });
